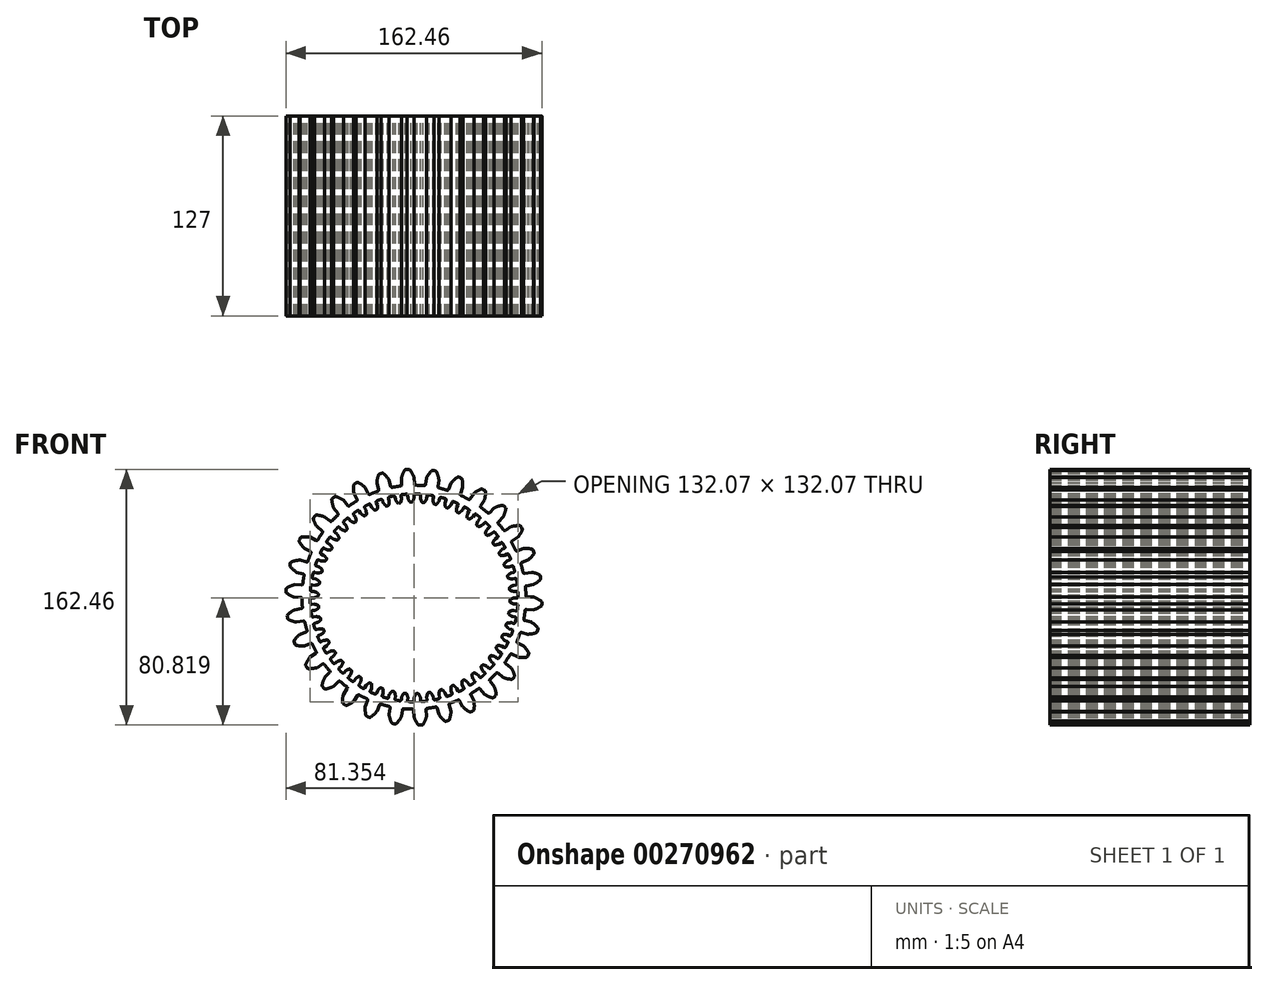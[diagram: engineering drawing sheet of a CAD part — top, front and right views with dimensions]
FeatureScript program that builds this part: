
annotation { "Feature Type Name" : "Feature", "Feature Type Description" : "" }
export const myFeature = defineFeature(function(context is Context, id is Id, definition is map)
    precondition{}
    {
        {
            var Q0;
            Q0=qCreatedBy(makeId("Front.planeOp"),FACE);
            var sketch = newSketch(context, id + "F0", { "sketchPlane" : qUnion([Q0])});
            skArc(sketch, "E0", {"start": v(-8.43, 70.62) * mm, "mid": v(-11.13, 70.24) * mm, "end": v(-13.8, 69.77) * mm});
            skArc(sketch, "E1.trimOffspring", {"start": v(0, 76.2) * mm, "mid": v(-1.15, 78.65) * mm, "end": v(-2.64, 80.92) * mm});
            skLineSegment(sketch, "E2", {"start": v(0, 76.2) * mm, "end": v(0.23, 71.86) * mm});
            skLineSegment(sketch, "E3", {"start": v(-3.26, 81.23) * mm, "end": v(-4.26, 81.23) * mm});
            skLineSegment(sketch, "E4.MirrorCS", {"start": v(-5.25, 81.13) * mm, "end": v(-4.26, 81.23) * mm});
            skArc(sketch, "E5.MirrorCS", {"start": v(-7.97, 75.78) * mm, "mid": v(-7.08, 78.34) * mm, "end": v(-5.84, 80.75) * mm});
            skLineSegment(sketch, "E6.MirrorCS", {"start": v(-7.97, 75.78) * mm, "end": v(-7.74, 71.44) * mm});
            skPoint(sketch, "E7.orphan", {"position": v(-7.45, 65.87) * mm});
            skPoint(sketch, "E8.orphan", {"position": v(0.52, 66.28) * mm});
            skPoint(sketch, "E9.visualSharp", {"position": v(-7.7, 70.7) * mm});
            skArc(sketch, "E9.filletArc", {"start": v(-8.43, 70.62) * mm, "mid": v(-7.92, 70.9) * mm, "end": v(-7.74, 71.44) * mm});
            skPoint(sketch, "E10.visualSharp", {"position": v(0.27, 71.12) * mm});
            skArc(sketch, "E10.filletArc", {"start": v(0.23, 71.86) * mm, "mid": v(0.47, 71.33) * mm, "end": v(1, 71.11) * mm});
            skPoint(sketch, "E11.visualSharp", {"position": v(-2.88, 81.23) * mm});
            skArc(sketch, "E11.filletArc", {"start": v(-2.64, 80.92) * mm, "mid": v(-2.91, 81.15) * mm, "end": v(-3.26, 81.23) * mm});
            skPoint(sketch, "E12.visualSharp", {"position": v(-5.63, 81.08) * mm});
            skArc(sketch, "E12.filletArc", {"start": v(-5.25, 81.13) * mm, "mid": v(-5.58, 81) * mm, "end": v(-5.84, 80.75) * mm});
            skArc(sketch, "E13.1.0", {"start": v(-22.93, 67.32) * mm, "mid": v(-22.49, 67.7) * mm, "end": v(-22.42, 68.27) * mm});
            skLineSegment(sketch, "E13.1.1", {"start": v(-23.55, 72.47) * mm, "end": v(-22.42, 68.27) * mm});
            skArc(sketch, "E13.1.2", {"start": v(-23.55, 72.47) * mm, "mid": v(-23.21, 75.16) * mm, "end": v(-22.5, 77.77) * mm});
            skArc(sketch, "E13.1.3", {"start": v(-22, 78.26) * mm, "mid": v(-22.3, 78.08) * mm, "end": v(-22.5, 77.77) * mm});
            skLineSegment(sketch, "E13.1.4", {"start": v(-22, 78.26) * mm, "end": v(-21.05, 78.57) * mm});
            skLineSegment(sketch, "E13.1.5", {"start": v(-20.08, 78.78) * mm, "end": v(-21.05, 78.57) * mm});
            skArc(sketch, "E13.1.6", {"start": v(-19.4, 78.6) * mm, "mid": v(-19.72, 78.77) * mm, "end": v(-20.08, 78.78) * mm});
            skArc(sketch, "E13.1.7", {"start": v(-15.84, 74.53) * mm, "mid": v(-17.48, 76.7) * mm, "end": v(-19.4, 78.6) * mm});
            skLineSegment(sketch, "E13.1.8", {"start": v(-15.84, 74.53) * mm, "end": v(-14.72, 70.34) * mm});
            skArc(sketch, "E13.1.9", {"start": v(-14.72, 70.34) * mm, "mid": v(-14.37, 69.87) * mm, "end": v(-13.8, 69.77) * mm});
            skArc(sketch, "E13.2.0", {"start": v(-36.42, 61.08) * mm, "mid": v(-36.07, 61.54) * mm, "end": v(-36.13, 62.12) * mm});
            skLineSegment(sketch, "E13.2.1", {"start": v(-38.1, 66) * mm, "end": v(-36.13, 62.12) * mm});
            skArc(sketch, "E13.2.2", {"start": v(-38.1, 66) * mm, "mid": v(-38.33, 68.7) * mm, "end": v(-38.18, 71.4) * mm});
            skArc(sketch, "E13.2.3", {"start": v(-37.79, 71.98) * mm, "mid": v(-38.05, 71.73) * mm, "end": v(-38.18, 71.4) * mm});
            skLineSegment(sketch, "E13.2.4", {"start": v(-37.79, 71.98) * mm, "end": v(-36.93, 72.47) * mm});
            skLineSegment(sketch, "E13.2.5", {"start": v(-36.02, 72.88) * mm, "end": v(-36.93, 72.47) * mm});
            skArc(sketch, "E13.2.6", {"start": v(-35.32, 72.85) * mm, "mid": v(-35.67, 72.95) * mm, "end": v(-36.02, 72.88) * mm});
            skArc(sketch, "E13.2.7", {"start": v(-31, 69.61) * mm, "mid": v(-33.04, 71.39) * mm, "end": v(-35.32, 72.85) * mm});
            skLineSegment(sketch, "E13.2.8", {"start": v(-31, 69.61) * mm, "end": v(-29.02, 65.74) * mm});
            skArc(sketch, "E13.2.9", {"start": v(-29.02, 65.74) * mm, "mid": v(-28.59, 65.36) * mm, "end": v(-28, 65.37) * mm});
            skArc(sketch, "E13.3.0", {"start": v(-48.33, 52.18) * mm, "mid": v(-48.08, 52.7) * mm, "end": v(-48.25, 53.25) * mm});
            skLineSegment(sketch, "E13.3.1", {"start": v(-50.99, 56.63) * mm, "end": v(-48.25, 53.25) * mm});
            skArc(sketch, "E13.3.2", {"start": v(-50.99, 56.63) * mm, "mid": v(-51.77, 59.22) * mm, "end": v(-52.19, 61.9) * mm});
            skArc(sketch, "E13.3.3", {"start": v(-51.93, 62.55) * mm, "mid": v(-52.13, 62.25) * mm, "end": v(-52.19, 61.9) * mm});
            skLineSegment(sketch, "E13.3.4", {"start": v(-51.93, 62.55) * mm, "end": v(-51.19, 63.21) * mm});
            skLineSegment(sketch, "E13.3.5", {"start": v(-50.38, 63.8) * mm, "end": v(-51.19, 63.21) * mm});
            skArc(sketch, "E13.3.6", {"start": v(-49.7, 63.92) * mm, "mid": v(-50.05, 63.94) * mm, "end": v(-50.38, 63.8) * mm});
            skArc(sketch, "E13.3.7", {"start": v(-44.79, 61.65) * mm, "mid": v(-47.16, 62.96) * mm, "end": v(-49.7, 63.92) * mm});
            skLineSegment(sketch, "E13.3.8", {"start": v(-44.79, 61.65) * mm, "end": v(-42.05, 58.27) * mm});
            skArc(sketch, "E13.3.9", {"start": v(-42.05, 58.27) * mm, "mid": v(-41.55, 57.98) * mm, "end": v(-40.99, 58.12) * mm});
            skArc(sketch, "E13.4.0", {"start": v(-58.12, 40.99) * mm, "mid": v(-57.98, 41.55) * mm, "end": v(-58.27, 42.05) * mm});
            skLineSegment(sketch, "E13.4.1", {"start": v(-61.65, 44.79) * mm, "end": v(-58.27, 42.05) * mm});
            skArc(sketch, "E13.4.2", {"start": v(-61.65, 44.79) * mm, "mid": v(-62.96, 47.16) * mm, "end": v(-63.92, 49.7) * mm});
            skArc(sketch, "E13.4.3", {"start": v(-63.8, 50.38) * mm, "mid": v(-63.94, 50.05) * mm, "end": v(-63.92, 49.7) * mm});
            skLineSegment(sketch, "E13.4.4", {"start": v(-63.8, 50.38) * mm, "end": v(-63.21, 51.19) * mm});
            skLineSegment(sketch, "E13.4.5", {"start": v(-62.55, 51.93) * mm, "end": v(-63.21, 51.19) * mm});
            skArc(sketch, "E13.4.6", {"start": v(-61.9, 52.19) * mm, "mid": v(-62.25, 52.13) * mm, "end": v(-62.55, 51.93) * mm});
            skArc(sketch, "E13.4.7", {"start": v(-56.63, 50.99) * mm, "mid": v(-59.22, 51.77) * mm, "end": v(-61.9, 52.19) * mm});
            skLineSegment(sketch, "E13.4.8", {"start": v(-56.63, 50.99) * mm, "end": v(-53.25, 48.25) * mm});
            skArc(sketch, "E13.4.9", {"start": v(-53.25, 48.25) * mm, "mid": v(-52.7, 48.08) * mm, "end": v(-52.18, 48.33) * mm});
            skArc(sketch, "E13.5.0", {"start": v(-65.37, 28) * mm, "mid": v(-65.36, 28.59) * mm, "end": v(-65.74, 29.02) * mm});
            skLineSegment(sketch, "E13.5.1", {"start": v(-69.61, 31) * mm, "end": v(-65.74, 29.02) * mm});
            skArc(sketch, "E13.5.2", {"start": v(-69.61, 31) * mm, "mid": v(-71.39, 33.04) * mm, "end": v(-72.85, 35.32) * mm});
            skArc(sketch, "E13.5.3", {"start": v(-72.88, 36.02) * mm, "mid": v(-72.95, 35.67) * mm, "end": v(-72.85, 35.32) * mm});
            skLineSegment(sketch, "E13.5.4", {"start": v(-72.88, 36.02) * mm, "end": v(-72.47, 36.93) * mm});
            skLineSegment(sketch, "E13.5.5", {"start": v(-71.98, 37.79) * mm, "end": v(-72.47, 36.93) * mm});
            skArc(sketch, "E13.5.6", {"start": v(-71.4, 38.18) * mm, "mid": v(-71.73, 38.05) * mm, "end": v(-71.98, 37.79) * mm});
            skArc(sketch, "E13.5.7", {"start": v(-66, 38.1) * mm, "mid": v(-68.7, 38.33) * mm, "end": v(-71.4, 38.18) * mm});
            skLineSegment(sketch, "E13.5.8", {"start": v(-66, 38.1) * mm, "end": v(-62.12, 36.13) * mm});
            skArc(sketch, "E13.5.9", {"start": v(-62.12, 36.13) * mm, "mid": v(-61.54, 36.07) * mm, "end": v(-61.08, 36.42) * mm});
            skArc(sketch, "E13.6.0", {"start": v(-69.77, 13.8) * mm, "mid": v(-69.87, 14.37) * mm, "end": v(-70.34, 14.72) * mm});
            skLineSegment(sketch, "E13.6.1", {"start": v(-74.53, 15.84) * mm, "end": v(-70.34, 14.72) * mm});
            skArc(sketch, "E13.6.2", {"start": v(-74.53, 15.84) * mm, "mid": v(-76.7, 17.48) * mm, "end": v(-78.6, 19.4) * mm});
            skArc(sketch, "E13.6.3", {"start": v(-78.78, 20.08) * mm, "mid": v(-78.77, 19.72) * mm, "end": v(-78.6, 19.4) * mm});
            skLineSegment(sketch, "E13.6.4", {"start": v(-78.78, 20.08) * mm, "end": v(-78.57, 21.05) * mm});
            skLineSegment(sketch, "E13.6.5", {"start": v(-78.26, 22) * mm, "end": v(-78.57, 21.05) * mm});
            skArc(sketch, "E13.6.6", {"start": v(-77.77, 22.5) * mm, "mid": v(-78.08, 22.3) * mm, "end": v(-78.26, 22) * mm});
            skArc(sketch, "E13.6.7", {"start": v(-72.47, 23.55) * mm, "mid": v(-75.16, 23.21) * mm, "end": v(-77.77, 22.5) * mm});
            skLineSegment(sketch, "E13.6.8", {"start": v(-72.47, 23.55) * mm, "end": v(-68.27, 22.42) * mm});
            skArc(sketch, "E13.6.9", {"start": v(-68.27, 22.42) * mm, "mid": v(-67.7, 22.49) * mm, "end": v(-67.32, 22.93) * mm});
            skArc(sketch, "E13.7.0", {"start": v(-71.11, -1) * mm, "mid": v(-71.33, -0.47) * mm, "end": v(-71.86, -0.23) * mm});
            skLineSegment(sketch, "E13.7.1", {"start": v(-76.2, 0) * mm, "end": v(-71.86, -0.23) * mm});
            skArc(sketch, "E13.7.2", {"start": v(-76.2, 0) * mm, "mid": v(-78.65, 1.15) * mm, "end": v(-80.92, 2.64) * mm});
            skArc(sketch, "E13.7.3", {"start": v(-81.23, 3.26) * mm, "mid": v(-81.15, 2.91) * mm, "end": v(-80.92, 2.64) * mm});
            skLineSegment(sketch, "E13.7.4", {"start": v(-81.23, 3.26) * mm, "end": v(-81.23, 4.26) * mm});
            skLineSegment(sketch, "E13.7.5", {"start": v(-81.13, 5.25) * mm, "end": v(-81.23, 4.26) * mm});
            skArc(sketch, "E13.7.6", {"start": v(-80.75, 5.84) * mm, "mid": v(-81, 5.58) * mm, "end": v(-81.13, 5.25) * mm});
            skArc(sketch, "E13.7.7", {"start": v(-75.78, 7.97) * mm, "mid": v(-78.34, 7.08) * mm, "end": v(-80.75, 5.84) * mm});
            skLineSegment(sketch, "E13.7.8", {"start": v(-75.78, 7.97) * mm, "end": v(-71.44, 7.74) * mm});
            skArc(sketch, "E13.7.9", {"start": v(-71.44, 7.74) * mm, "mid": v(-70.9, 7.92) * mm, "end": v(-70.62, 8.43) * mm});
            skArc(sketch, "E13.8.0", {"start": v(-69.35, -15.77) * mm, "mid": v(-69.68, -15.29) * mm, "end": v(-70.24, -15.16) * mm});
            skLineSegment(sketch, "E13.8.1", {"start": v(-74.53, -15.84) * mm, "end": v(-70.24, -15.16) * mm});
            skArc(sketch, "E13.8.2", {"start": v(-74.53, -15.84) * mm, "mid": v(-77.17, -15.23) * mm, "end": v(-79.7, -14.24) * mm});
            skArc(sketch, "E13.8.3", {"start": v(-80.13, -13.7) * mm, "mid": v(-79.98, -14.02) * mm, "end": v(-79.7, -14.24) * mm});
            skLineSegment(sketch, "E13.8.4", {"start": v(-80.13, -13.7) * mm, "end": v(-80.34, -12.72) * mm});
            skLineSegment(sketch, "E13.8.5", {"start": v(-80.44, -11.74) * mm, "end": v(-80.34, -12.72) * mm});
            skArc(sketch, "E13.8.6", {"start": v(-80.2, -11.08) * mm, "mid": v(-80.4, -11.38) * mm, "end": v(-80.44, -11.74) * mm});
            skArc(sketch, "E13.8.7", {"start": v(-75.78, -7.97) * mm, "mid": v(-78.1, -9.37) * mm, "end": v(-80.2, -11.08) * mm});
            skLineSegment(sketch, "E13.8.8", {"start": v(-75.78, -7.97) * mm, "end": v(-71.49, -7.29) * mm});
            skArc(sketch, "E13.8.9", {"start": v(-71.49, -7.29) * mm, "mid": v(-71, -7) * mm, "end": v(-70.83, -6.44) * mm});
            skArc(sketch, "E13.9.0", {"start": v(-64.56, -29.84) * mm, "mid": v(-64.98, -29.44) * mm, "end": v(-65.55, -29.44) * mm});
            skLineSegment(sketch, "E13.9.1", {"start": v(-69.61, -31) * mm, "end": v(-65.55, -29.44) * mm});
            skArc(sketch, "E13.9.2", {"start": v(-69.61, -31) * mm, "mid": v(-72.32, -30.94) * mm, "end": v(-75, -30.5) * mm});
            skArc(sketch, "E13.9.3", {"start": v(-75.53, -30.06) * mm, "mid": v(-75.32, -30.34) * mm, "end": v(-75, -30.5) * mm});
            skLineSegment(sketch, "E13.9.4", {"start": v(-75.53, -30.06) * mm, "end": v(-75.94, -29.15) * mm});
            skLineSegment(sketch, "E13.9.5", {"start": v(-76.25, -28.2) * mm, "end": v(-75.94, -29.15) * mm});
            skArc(sketch, "E13.9.6", {"start": v(-76.14, -27.51) * mm, "mid": v(-76.28, -27.85) * mm, "end": v(-76.25, -28.2) * mm});
            skArc(sketch, "E13.9.7", {"start": v(-72.47, -23.55) * mm, "mid": v(-74.45, -25.4) * mm, "end": v(-76.14, -27.51) * mm});
            skLineSegment(sketch, "E13.9.8", {"start": v(-72.47, -23.55) * mm, "end": v(-68.41, -21.99) * mm});
            skArc(sketch, "E13.9.9", {"start": v(-68.41, -21.99) * mm, "mid": v(-67.99, -21.6) * mm, "end": v(-67.94, -21.02) * mm});
            skArc(sketch, "E13.10.0", {"start": v(-56.94, -42.61) * mm, "mid": v(-57.43, -42.3) * mm, "end": v(-58, -42.42) * mm});
            skLineSegment(sketch, "E13.10.1", {"start": v(-61.65, -44.79) * mm, "end": v(-58, -42.42) * mm});
            skArc(sketch, "E13.10.2", {"start": v(-61.65, -44.79) * mm, "mid": v(-64.3, -45.3) * mm, "end": v(-67.01, -45.43) * mm});
            skArc(sketch, "E13.10.3", {"start": v(-67.63, -45.1) * mm, "mid": v(-67.36, -45.34) * mm, "end": v(-67.01, -45.43) * mm});
            skLineSegment(sketch, "E13.10.4", {"start": v(-67.63, -45.1) * mm, "end": v(-68.22, -44.3) * mm});
            skLineSegment(sketch, "E13.10.5", {"start": v(-68.72, -43.44) * mm, "end": v(-68.22, -44.3) * mm});
            skArc(sketch, "E13.10.6", {"start": v(-68.76, -42.74) * mm, "mid": v(-68.82, -43.1) * mm, "end": v(-68.72, -43.44) * mm});
            skArc(sketch, "E13.10.7", {"start": v(-66, -38.1) * mm, "mid": v(-67.54, -40.32) * mm, "end": v(-68.76, -42.74) * mm});
            skLineSegment(sketch, "E13.10.8", {"start": v(-66, -38.1) * mm, "end": v(-62.35, -35.73) * mm});
            skArc(sketch, "E13.10.9", {"start": v(-62.35, -35.73) * mm, "mid": v(-62.01, -35.26) * mm, "end": v(-62.09, -34.69) * mm});
            skArc(sketch, "E13.11.0", {"start": v(-46.84, -53.52) * mm, "mid": v(-47.38, -53.32) * mm, "end": v(-47.91, -53.55) * mm});
            skLineSegment(sketch, "E13.11.1", {"start": v(-50.99, -56.63) * mm, "end": v(-47.91, -53.55) * mm});
            skArc(sketch, "E13.11.2", {"start": v(-50.99, -56.63) * mm, "mid": v(-53.48, -57.68) * mm, "end": v(-56.1, -58.37) * mm});
            skArc(sketch, "E13.11.3", {"start": v(-56.78, -58.18) * mm, "mid": v(-56.46, -58.35) * mm, "end": v(-56.1, -58.37) * mm});
            skLineSegment(sketch, "E13.11.4", {"start": v(-56.78, -58.18) * mm, "end": v(-57.52, -57.52) * mm});
            skLineSegment(sketch, "E13.11.5", {"start": v(-58.18, -56.78) * mm, "end": v(-57.52, -57.52) * mm});
            skArc(sketch, "E13.11.6", {"start": v(-58.37, -56.1) * mm, "mid": v(-58.35, -56.46) * mm, "end": v(-58.18, -56.78) * mm});
            skArc(sketch, "E13.11.7", {"start": v(-56.63, -50.99) * mm, "mid": v(-57.68, -53.48) * mm, "end": v(-58.37, -56.1) * mm});
            skLineSegment(sketch, "E13.11.8", {"start": v(-56.63, -50.99) * mm, "end": v(-53.55, -47.91) * mm});
            skArc(sketch, "E13.11.9", {"start": v(-53.55, -47.91) * mm, "mid": v(-53.32, -47.38) * mm, "end": v(-53.52, -46.84) * mm});
            skArc(sketch, "E13.12.0", {"start": v(-34.69, -62.09) * mm, "mid": v(-35.26, -62.01) * mm, "end": v(-35.73, -62.35) * mm});
            skLineSegment(sketch, "E13.12.1", {"start": v(-38.1, -66) * mm, "end": v(-35.73, -62.35) * mm});
            skArc(sketch, "E13.12.2", {"start": v(-38.1, -66) * mm, "mid": v(-40.32, -67.54) * mm, "end": v(-42.74, -68.76) * mm});
            skArc(sketch, "E13.12.3", {"start": v(-43.44, -68.72) * mm, "mid": v(-43.1, -68.82) * mm, "end": v(-42.74, -68.76) * mm});
            skLineSegment(sketch, "E13.12.4", {"start": v(-43.44, -68.72) * mm, "end": v(-44.3, -68.22) * mm});
            skLineSegment(sketch, "E13.12.5", {"start": v(-45.1, -67.63) * mm, "end": v(-44.3, -68.22) * mm});
            skArc(sketch, "E13.12.6", {"start": v(-45.43, -67.01) * mm, "mid": v(-45.34, -67.36) * mm, "end": v(-45.1, -67.63) * mm});
            skArc(sketch, "E13.12.7", {"start": v(-44.79, -61.65) * mm, "mid": v(-45.3, -64.3) * mm, "end": v(-45.43, -67.01) * mm});
            skLineSegment(sketch, "E13.12.8", {"start": v(-44.79, -61.65) * mm, "end": v(-42.42, -58) * mm});
            skArc(sketch, "E13.12.9", {"start": v(-42.42, -58) * mm, "mid": v(-42.3, -57.43) * mm, "end": v(-42.61, -56.94) * mm});
            skArc(sketch, "E13.13.0", {"start": v(-21.02, -67.94) * mm, "mid": v(-21.6, -67.99) * mm, "end": v(-21.99, -68.41) * mm});
            skLineSegment(sketch, "E13.13.1", {"start": v(-23.55, -72.47) * mm, "end": v(-21.99, -68.41) * mm});
            skArc(sketch, "E13.13.2", {"start": v(-23.55, -72.47) * mm, "mid": v(-25.4, -74.45) * mm, "end": v(-27.51, -76.14) * mm});
            skArc(sketch, "E13.13.3", {"start": v(-28.2, -76.25) * mm, "mid": v(-27.85, -76.28) * mm, "end": v(-27.51, -76.14) * mm});
            skLineSegment(sketch, "E13.13.4", {"start": v(-28.2, -76.25) * mm, "end": v(-29.15, -75.94) * mm});
            skLineSegment(sketch, "E13.13.5", {"start": v(-30.06, -75.53) * mm, "end": v(-29.15, -75.94) * mm});
            skArc(sketch, "E13.13.6", {"start": v(-30.5, -75) * mm, "mid": v(-30.34, -75.32) * mm, "end": v(-30.06, -75.53) * mm});
            skArc(sketch, "E13.13.7", {"start": v(-31, -69.61) * mm, "mid": v(-30.94, -72.32) * mm, "end": v(-30.5, -75) * mm});
            skLineSegment(sketch, "E13.13.8", {"start": v(-31, -69.61) * mm, "end": v(-29.44, -65.55) * mm});
            skArc(sketch, "E13.13.9", {"start": v(-29.44, -65.55) * mm, "mid": v(-29.44, -64.98) * mm, "end": v(-29.84, -64.56) * mm});
            skArc(sketch, "E13.14.0", {"start": v(-6.44, -70.83) * mm, "mid": v(-7, -71) * mm, "end": v(-7.29, -71.49) * mm});
            skLineSegment(sketch, "E13.14.1", {"start": v(-7.97, -75.78) * mm, "end": v(-7.29, -71.49) * mm});
            skArc(sketch, "E13.14.2", {"start": v(-7.97, -75.78) * mm, "mid": v(-9.37, -78.1) * mm, "end": v(-11.08, -80.2) * mm});
            skArc(sketch, "E13.14.3", {"start": v(-11.74, -80.44) * mm, "mid": v(-11.38, -80.4) * mm, "end": v(-11.08, -80.2) * mm});
            skLineSegment(sketch, "E13.14.4", {"start": v(-11.74, -80.44) * mm, "end": v(-12.72, -80.34) * mm});
            skLineSegment(sketch, "E13.14.5", {"start": v(-13.7, -80.13) * mm, "end": v(-12.72, -80.34) * mm});
            skArc(sketch, "E13.14.6", {"start": v(-14.24, -79.7) * mm, "mid": v(-14.02, -79.98) * mm, "end": v(-13.7, -80.13) * mm});
            skArc(sketch, "E13.14.7", {"start": v(-15.84, -74.53) * mm, "mid": v(-15.23, -77.17) * mm, "end": v(-14.24, -79.7) * mm});
            skLineSegment(sketch, "E13.14.8", {"start": v(-15.84, -74.53) * mm, "end": v(-15.16, -70.24) * mm});
            skArc(sketch, "E13.14.9", {"start": v(-15.16, -70.24) * mm, "mid": v(-15.29, -69.68) * mm, "end": v(-15.77, -69.35) * mm});
            skArc(sketch, "E13.15.0", {"start": v(8.43, -70.62) * mm, "mid": v(7.92, -70.9) * mm, "end": v(7.74, -71.44) * mm});
            skLineSegment(sketch, "E13.15.1", {"start": v(7.97, -75.78) * mm, "end": v(7.74, -71.44) * mm});
            skArc(sketch, "E13.15.2", {"start": v(7.97, -75.78) * mm, "mid": v(7.08, -78.34) * mm, "end": v(5.84, -80.75) * mm});
            skArc(sketch, "E13.15.3", {"start": v(5.25, -81.13) * mm, "mid": v(5.58, -81) * mm, "end": v(5.84, -80.75) * mm});
            skLineSegment(sketch, "E13.15.4", {"start": v(5.25, -81.13) * mm, "end": v(4.26, -81.23) * mm});
            skLineSegment(sketch, "E13.15.5", {"start": v(3.26, -81.23) * mm, "end": v(4.26, -81.23) * mm});
            skArc(sketch, "E13.15.6", {"start": v(2.64, -80.92) * mm, "mid": v(2.91, -81.15) * mm, "end": v(3.26, -81.23) * mm});
            skArc(sketch, "E13.15.7", {"start": v(0, -76.2) * mm, "mid": v(1.15, -78.65) * mm, "end": v(2.64, -80.92) * mm});
            skLineSegment(sketch, "E13.15.8", {"start": v(0, -76.2) * mm, "end": v(-0.23, -71.86) * mm});
            skArc(sketch, "E13.15.9", {"start": v(-0.23, -71.86) * mm, "mid": v(-0.47, -71.33) * mm, "end": v(-1, -71.11) * mm});
            skArc(sketch, "E13.16.0", {"start": v(22.93, -67.32) * mm, "mid": v(22.49, -67.7) * mm, "end": v(22.42, -68.27) * mm});
            skLineSegment(sketch, "E13.16.1", {"start": v(23.55, -72.47) * mm, "end": v(22.42, -68.27) * mm});
            skArc(sketch, "E13.16.2", {"start": v(23.55, -72.47) * mm, "mid": v(23.21, -75.16) * mm, "end": v(22.5, -77.77) * mm});
            skArc(sketch, "E13.16.3", {"start": v(22, -78.26) * mm, "mid": v(22.3, -78.08) * mm, "end": v(22.5, -77.77) * mm});
            skLineSegment(sketch, "E13.16.4", {"start": v(22, -78.26) * mm, "end": v(21.05, -78.57) * mm});
            skLineSegment(sketch, "E13.16.5", {"start": v(20.08, -78.78) * mm, "end": v(21.05, -78.57) * mm});
            skArc(sketch, "E13.16.6", {"start": v(19.4, -78.6) * mm, "mid": v(19.72, -78.77) * mm, "end": v(20.08, -78.78) * mm});
            skArc(sketch, "E13.16.7", {"start": v(15.84, -74.53) * mm, "mid": v(17.48, -76.7) * mm, "end": v(19.4, -78.6) * mm});
            skLineSegment(sketch, "E13.16.8", {"start": v(15.84, -74.53) * mm, "end": v(14.72, -70.34) * mm});
            skArc(sketch, "E13.16.9", {"start": v(14.72, -70.34) * mm, "mid": v(14.37, -69.87) * mm, "end": v(13.8, -69.77) * mm});
            skArc(sketch, "E13.17.0", {"start": v(36.42, -61.08) * mm, "mid": v(36.07, -61.54) * mm, "end": v(36.13, -62.12) * mm});
            skLineSegment(sketch, "E13.17.1", {"start": v(38.1, -66) * mm, "end": v(36.13, -62.12) * mm});
            skArc(sketch, "E13.17.2", {"start": v(38.1, -66) * mm, "mid": v(38.33, -68.7) * mm, "end": v(38.18, -71.4) * mm});
            skArc(sketch, "E13.17.3", {"start": v(37.79, -71.98) * mm, "mid": v(38.05, -71.73) * mm, "end": v(38.18, -71.4) * mm});
            skLineSegment(sketch, "E13.17.4", {"start": v(37.79, -71.98) * mm, "end": v(36.93, -72.47) * mm});
            skLineSegment(sketch, "E13.17.5", {"start": v(36.02, -72.88) * mm, "end": v(36.93, -72.47) * mm});
            skArc(sketch, "E13.17.6", {"start": v(35.32, -72.85) * mm, "mid": v(35.67, -72.95) * mm, "end": v(36.02, -72.88) * mm});
            skArc(sketch, "E13.17.7", {"start": v(31, -69.61) * mm, "mid": v(33.04, -71.39) * mm, "end": v(35.32, -72.85) * mm});
            skLineSegment(sketch, "E13.17.8", {"start": v(31, -69.61) * mm, "end": v(29.02, -65.74) * mm});
            skArc(sketch, "E13.17.9", {"start": v(29.02, -65.74) * mm, "mid": v(28.59, -65.36) * mm, "end": v(28, -65.37) * mm});
            skArc(sketch, "E13.18.0", {"start": v(48.33, -52.18) * mm, "mid": v(48.08, -52.7) * mm, "end": v(48.25, -53.25) * mm});
            skLineSegment(sketch, "E13.18.1", {"start": v(50.99, -56.63) * mm, "end": v(48.25, -53.25) * mm});
            skArc(sketch, "E13.18.2", {"start": v(50.99, -56.63) * mm, "mid": v(51.77, -59.22) * mm, "end": v(52.19, -61.9) * mm});
            skArc(sketch, "E13.18.3", {"start": v(51.93, -62.55) * mm, "mid": v(52.13, -62.25) * mm, "end": v(52.19, -61.9) * mm});
            skLineSegment(sketch, "E13.18.4", {"start": v(51.93, -62.55) * mm, "end": v(51.19, -63.21) * mm});
            skLineSegment(sketch, "E13.18.5", {"start": v(50.38, -63.8) * mm, "end": v(51.19, -63.21) * mm});
            skArc(sketch, "E13.18.6", {"start": v(49.7, -63.92) * mm, "mid": v(50.05, -63.94) * mm, "end": v(50.38, -63.8) * mm});
            skArc(sketch, "E13.18.7", {"start": v(44.79, -61.65) * mm, "mid": v(47.16, -62.96) * mm, "end": v(49.7, -63.92) * mm});
            skLineSegment(sketch, "E13.18.8", {"start": v(44.79, -61.65) * mm, "end": v(42.05, -58.27) * mm});
            skArc(sketch, "E13.18.9", {"start": v(42.05, -58.27) * mm, "mid": v(41.55, -57.98) * mm, "end": v(40.99, -58.12) * mm});
            skArc(sketch, "E13.19.0", {"start": v(58.12, -40.99) * mm, "mid": v(57.98, -41.55) * mm, "end": v(58.27, -42.05) * mm});
            skLineSegment(sketch, "E13.19.1", {"start": v(61.65, -44.79) * mm, "end": v(58.27, -42.05) * mm});
            skArc(sketch, "E13.19.2", {"start": v(61.65, -44.79) * mm, "mid": v(62.96, -47.16) * mm, "end": v(63.92, -49.7) * mm});
            skArc(sketch, "E13.19.3", {"start": v(63.8, -50.38) * mm, "mid": v(63.94, -50.05) * mm, "end": v(63.92, -49.7) * mm});
            skLineSegment(sketch, "E13.19.4", {"start": v(63.8, -50.38) * mm, "end": v(63.21, -51.19) * mm});
            skLineSegment(sketch, "E13.19.5", {"start": v(62.55, -51.93) * mm, "end": v(63.21, -51.19) * mm});
            skArc(sketch, "E13.19.6", {"start": v(61.9, -52.19) * mm, "mid": v(62.25, -52.13) * mm, "end": v(62.55, -51.93) * mm});
            skArc(sketch, "E13.19.7", {"start": v(56.63, -50.99) * mm, "mid": v(59.22, -51.77) * mm, "end": v(61.9, -52.19) * mm});
            skLineSegment(sketch, "E13.19.8", {"start": v(56.63, -50.99) * mm, "end": v(53.25, -48.25) * mm});
            skArc(sketch, "E13.19.9", {"start": v(53.25, -48.25) * mm, "mid": v(52.7, -48.08) * mm, "end": v(52.18, -48.33) * mm});
            skArc(sketch, "E13.20.0", {"start": v(65.37, -28) * mm, "mid": v(65.36, -28.59) * mm, "end": v(65.74, -29.02) * mm});
            skLineSegment(sketch, "E13.20.1", {"start": v(69.61, -31) * mm, "end": v(65.74, -29.02) * mm});
            skArc(sketch, "E13.20.2", {"start": v(69.61, -31) * mm, "mid": v(71.39, -33.04) * mm, "end": v(72.85, -35.32) * mm});
            skArc(sketch, "E13.20.3", {"start": v(72.88, -36.02) * mm, "mid": v(72.95, -35.67) * mm, "end": v(72.85, -35.32) * mm});
            skLineSegment(sketch, "E13.20.4", {"start": v(72.88, -36.02) * mm, "end": v(72.47, -36.93) * mm});
            skLineSegment(sketch, "E13.20.5", {"start": v(71.98, -37.79) * mm, "end": v(72.47, -36.93) * mm});
            skArc(sketch, "E13.20.6", {"start": v(71.4, -38.18) * mm, "mid": v(71.73, -38.05) * mm, "end": v(71.98, -37.79) * mm});
            skArc(sketch, "E13.20.7", {"start": v(66, -38.1) * mm, "mid": v(68.7, -38.33) * mm, "end": v(71.4, -38.18) * mm});
            skLineSegment(sketch, "E13.20.8", {"start": v(66, -38.1) * mm, "end": v(62.12, -36.13) * mm});
            skArc(sketch, "E13.20.9", {"start": v(62.12, -36.13) * mm, "mid": v(61.54, -36.07) * mm, "end": v(61.08, -36.42) * mm});
            skArc(sketch, "E13.21.0", {"start": v(69.77, -13.8) * mm, "mid": v(69.87, -14.37) * mm, "end": v(70.34, -14.72) * mm});
            skLineSegment(sketch, "E13.21.1", {"start": v(74.53, -15.84) * mm, "end": v(70.34, -14.72) * mm});
            skArc(sketch, "E13.21.2", {"start": v(74.53, -15.84) * mm, "mid": v(76.7, -17.48) * mm, "end": v(78.6, -19.4) * mm});
            skArc(sketch, "E13.21.3", {"start": v(78.78, -20.08) * mm, "mid": v(78.77, -19.72) * mm, "end": v(78.6, -19.4) * mm});
            skLineSegment(sketch, "E13.21.4", {"start": v(78.78, -20.08) * mm, "end": v(78.57, -21.05) * mm});
            skLineSegment(sketch, "E13.21.5", {"start": v(78.26, -22) * mm, "end": v(78.57, -21.05) * mm});
            skArc(sketch, "E13.21.6", {"start": v(77.77, -22.5) * mm, "mid": v(78.08, -22.3) * mm, "end": v(78.26, -22) * mm});
            skArc(sketch, "E13.21.7", {"start": v(72.47, -23.55) * mm, "mid": v(75.16, -23.21) * mm, "end": v(77.77, -22.5) * mm});
            skLineSegment(sketch, "E13.21.8", {"start": v(72.47, -23.55) * mm, "end": v(68.27, -22.42) * mm});
            skArc(sketch, "E13.21.9", {"start": v(68.27, -22.42) * mm, "mid": v(67.7, -22.49) * mm, "end": v(67.32, -22.93) * mm});
            skArc(sketch, "E13.22.0", {"start": v(71.11, 1) * mm, "mid": v(71.33, 0.47) * mm, "end": v(71.86, 0.23) * mm});
            skLineSegment(sketch, "E13.22.1", {"start": v(76.2, 0) * mm, "end": v(71.86, 0.23) * mm});
            skArc(sketch, "E13.22.2", {"start": v(76.2, 0) * mm, "mid": v(78.65, -1.15) * mm, "end": v(80.92, -2.64) * mm});
            skArc(sketch, "E13.22.3", {"start": v(81.23, -3.26) * mm, "mid": v(81.15, -2.91) * mm, "end": v(80.92, -2.64) * mm});
            skLineSegment(sketch, "E13.22.4", {"start": v(81.23, -3.26) * mm, "end": v(81.23, -4.26) * mm});
            skLineSegment(sketch, "E13.22.5", {"start": v(81.13, -5.25) * mm, "end": v(81.23, -4.26) * mm});
            skArc(sketch, "E13.22.6", {"start": v(80.75, -5.84) * mm, "mid": v(81, -5.58) * mm, "end": v(81.13, -5.25) * mm});
            skArc(sketch, "E13.22.7", {"start": v(75.78, -7.97) * mm, "mid": v(78.34, -7.08) * mm, "end": v(80.75, -5.84) * mm});
            skLineSegment(sketch, "E13.22.8", {"start": v(75.78, -7.97) * mm, "end": v(71.44, -7.74) * mm});
            skArc(sketch, "E13.22.9", {"start": v(71.44, -7.74) * mm, "mid": v(70.9, -7.92) * mm, "end": v(70.62, -8.43) * mm});
            skArc(sketch, "E13.23.0", {"start": v(69.35, 15.77) * mm, "mid": v(69.68, 15.29) * mm, "end": v(70.24, 15.16) * mm});
            skLineSegment(sketch, "E13.23.1", {"start": v(74.53, 15.84) * mm, "end": v(70.24, 15.16) * mm});
            skArc(sketch, "E13.23.2", {"start": v(74.53, 15.84) * mm, "mid": v(77.17, 15.23) * mm, "end": v(79.7, 14.24) * mm});
            skArc(sketch, "E13.23.3", {"start": v(80.13, 13.7) * mm, "mid": v(79.98, 14.02) * mm, "end": v(79.7, 14.24) * mm});
            skLineSegment(sketch, "E13.23.4", {"start": v(80.13, 13.7) * mm, "end": v(80.34, 12.72) * mm});
            skLineSegment(sketch, "E13.23.5", {"start": v(80.44, 11.74) * mm, "end": v(80.34, 12.72) * mm});
            skArc(sketch, "E13.23.6", {"start": v(80.2, 11.08) * mm, "mid": v(80.4, 11.38) * mm, "end": v(80.44, 11.74) * mm});
            skArc(sketch, "E13.23.7", {"start": v(75.78, 7.97) * mm, "mid": v(78.1, 9.37) * mm, "end": v(80.2, 11.08) * mm});
            skLineSegment(sketch, "E13.23.8", {"start": v(75.78, 7.97) * mm, "end": v(71.49, 7.29) * mm});
            skArc(sketch, "E13.23.9", {"start": v(71.49, 7.29) * mm, "mid": v(71, 7) * mm, "end": v(70.83, 6.44) * mm});
            skArc(sketch, "E13.24.0", {"start": v(64.56, 29.84) * mm, "mid": v(64.98, 29.44) * mm, "end": v(65.55, 29.44) * mm});
            skLineSegment(sketch, "E13.24.1", {"start": v(69.61, 31) * mm, "end": v(65.55, 29.44) * mm});
            skArc(sketch, "E13.24.2", {"start": v(69.61, 31) * mm, "mid": v(72.32, 30.94) * mm, "end": v(75, 30.5) * mm});
            skArc(sketch, "E13.24.3", {"start": v(75.53, 30.06) * mm, "mid": v(75.32, 30.34) * mm, "end": v(75, 30.5) * mm});
            skLineSegment(sketch, "E13.24.4", {"start": v(75.53, 30.06) * mm, "end": v(75.94, 29.15) * mm});
            skLineSegment(sketch, "E13.24.5", {"start": v(76.25, 28.2) * mm, "end": v(75.94, 29.15) * mm});
            skArc(sketch, "E13.24.6", {"start": v(76.14, 27.51) * mm, "mid": v(76.28, 27.85) * mm, "end": v(76.25, 28.2) * mm});
            skArc(sketch, "E13.24.7", {"start": v(72.47, 23.55) * mm, "mid": v(74.45, 25.4) * mm, "end": v(76.14, 27.51) * mm});
            skLineSegment(sketch, "E13.24.8", {"start": v(72.47, 23.55) * mm, "end": v(68.41, 21.99) * mm});
            skArc(sketch, "E13.24.9", {"start": v(68.41, 21.99) * mm, "mid": v(67.99, 21.6) * mm, "end": v(67.94, 21.02) * mm});
            skArc(sketch, "E13.25.0", {"start": v(56.94, 42.61) * mm, "mid": v(57.43, 42.3) * mm, "end": v(58, 42.42) * mm});
            skLineSegment(sketch, "E13.25.1", {"start": v(61.65, 44.79) * mm, "end": v(58, 42.42) * mm});
            skArc(sketch, "E13.25.2", {"start": v(61.65, 44.79) * mm, "mid": v(64.3, 45.3) * mm, "end": v(67.01, 45.43) * mm});
            skArc(sketch, "E13.25.3", {"start": v(67.63, 45.1) * mm, "mid": v(67.36, 45.34) * mm, "end": v(67.01, 45.43) * mm});
            skLineSegment(sketch, "E13.25.4", {"start": v(67.63, 45.1) * mm, "end": v(68.22, 44.3) * mm});
            skLineSegment(sketch, "E13.25.5", {"start": v(68.72, 43.44) * mm, "end": v(68.22, 44.3) * mm});
            skArc(sketch, "E13.25.6", {"start": v(68.76, 42.74) * mm, "mid": v(68.82, 43.1) * mm, "end": v(68.72, 43.44) * mm});
            skArc(sketch, "E13.25.7", {"start": v(66, 38.1) * mm, "mid": v(67.54, 40.32) * mm, "end": v(68.76, 42.74) * mm});
            skLineSegment(sketch, "E13.25.8", {"start": v(66, 38.1) * mm, "end": v(62.35, 35.73) * mm});
            skArc(sketch, "E13.25.9", {"start": v(62.35, 35.73) * mm, "mid": v(62.01, 35.26) * mm, "end": v(62.09, 34.69) * mm});
            skArc(sketch, "E13.26.0", {"start": v(46.84, 53.52) * mm, "mid": v(47.38, 53.32) * mm, "end": v(47.91, 53.55) * mm});
            skLineSegment(sketch, "E13.26.1", {"start": v(50.99, 56.63) * mm, "end": v(47.91, 53.55) * mm});
            skArc(sketch, "E13.26.2", {"start": v(50.99, 56.63) * mm, "mid": v(53.48, 57.68) * mm, "end": v(56.1, 58.37) * mm});
            skArc(sketch, "E13.26.3", {"start": v(56.78, 58.18) * mm, "mid": v(56.46, 58.35) * mm, "end": v(56.1, 58.37) * mm});
            skLineSegment(sketch, "E13.26.4", {"start": v(56.78, 58.18) * mm, "end": v(57.52, 57.52) * mm});
            skLineSegment(sketch, "E13.26.5", {"start": v(58.18, 56.78) * mm, "end": v(57.52, 57.52) * mm});
            skArc(sketch, "E13.26.6", {"start": v(58.37, 56.1) * mm, "mid": v(58.35, 56.46) * mm, "end": v(58.18, 56.78) * mm});
            skArc(sketch, "E13.26.7", {"start": v(56.63, 50.99) * mm, "mid": v(57.68, 53.48) * mm, "end": v(58.37, 56.1) * mm});
            skLineSegment(sketch, "E13.26.8", {"start": v(56.63, 50.99) * mm, "end": v(53.55, 47.91) * mm});
            skArc(sketch, "E13.26.9", {"start": v(53.55, 47.91) * mm, "mid": v(53.32, 47.38) * mm, "end": v(53.52, 46.84) * mm});
            skArc(sketch, "E13.27.0", {"start": v(34.69, 62.09) * mm, "mid": v(35.26, 62.01) * mm, "end": v(35.73, 62.35) * mm});
            skLineSegment(sketch, "E13.27.1", {"start": v(38.1, 66) * mm, "end": v(35.73, 62.35) * mm});
            skArc(sketch, "E13.27.2", {"start": v(38.1, 66) * mm, "mid": v(40.32, 67.54) * mm, "end": v(42.74, 68.76) * mm});
            skArc(sketch, "E13.27.3", {"start": v(43.44, 68.72) * mm, "mid": v(43.1, 68.82) * mm, "end": v(42.74, 68.76) * mm});
            skLineSegment(sketch, "E13.27.4", {"start": v(43.44, 68.72) * mm, "end": v(44.3, 68.22) * mm});
            skLineSegment(sketch, "E13.27.5", {"start": v(45.1, 67.63) * mm, "end": v(44.3, 68.22) * mm});
            skArc(sketch, "E13.27.6", {"start": v(45.43, 67.01) * mm, "mid": v(45.34, 67.36) * mm, "end": v(45.1, 67.63) * mm});
            skArc(sketch, "E13.27.7", {"start": v(44.79, 61.65) * mm, "mid": v(45.3, 64.3) * mm, "end": v(45.43, 67.01) * mm});
            skLineSegment(sketch, "E13.27.8", {"start": v(44.79, 61.65) * mm, "end": v(42.42, 58) * mm});
            skArc(sketch, "E13.27.9", {"start": v(42.42, 58) * mm, "mid": v(42.3, 57.43) * mm, "end": v(42.61, 56.94) * mm});
            skArc(sketch, "E13.28.0", {"start": v(21.02, 67.94) * mm, "mid": v(21.6, 67.99) * mm, "end": v(21.99, 68.41) * mm});
            skLineSegment(sketch, "E13.28.1", {"start": v(23.55, 72.47) * mm, "end": v(21.99, 68.41) * mm});
            skArc(sketch, "E13.28.2", {"start": v(23.55, 72.47) * mm, "mid": v(25.4, 74.45) * mm, "end": v(27.51, 76.14) * mm});
            skArc(sketch, "E13.28.3", {"start": v(28.2, 76.25) * mm, "mid": v(27.85, 76.28) * mm, "end": v(27.51, 76.14) * mm});
            skLineSegment(sketch, "E13.28.4", {"start": v(28.2, 76.25) * mm, "end": v(29.15, 75.94) * mm});
            skLineSegment(sketch, "E13.28.5", {"start": v(30.06, 75.53) * mm, "end": v(29.15, 75.94) * mm});
            skArc(sketch, "E13.28.6", {"start": v(30.5, 75) * mm, "mid": v(30.34, 75.32) * mm, "end": v(30.06, 75.53) * mm});
            skArc(sketch, "E13.28.7", {"start": v(31, 69.61) * mm, "mid": v(30.94, 72.32) * mm, "end": v(30.5, 75) * mm});
            skLineSegment(sketch, "E13.28.8", {"start": v(31, 69.61) * mm, "end": v(29.44, 65.55) * mm});
            skArc(sketch, "E13.28.9", {"start": v(29.44, 65.55) * mm, "mid": v(29.44, 64.98) * mm, "end": v(29.84, 64.56) * mm});
            skArc(sketch, "E13.29.0", {"start": v(6.44, 70.83) * mm, "mid": v(7, 71) * mm, "end": v(7.29, 71.49) * mm});
            skLineSegment(sketch, "E13.29.1", {"start": v(7.97, 75.78) * mm, "end": v(7.29, 71.49) * mm});
            skArc(sketch, "E13.29.2", {"start": v(7.97, 75.78) * mm, "mid": v(9.37, 78.1) * mm, "end": v(11.08, 80.2) * mm});
            skArc(sketch, "E13.29.3", {"start": v(11.74, 80.44) * mm, "mid": v(11.38, 80.4) * mm, "end": v(11.08, 80.2) * mm});
            skLineSegment(sketch, "E13.29.4", {"start": v(11.74, 80.44) * mm, "end": v(12.72, 80.34) * mm});
            skLineSegment(sketch, "E13.29.5", {"start": v(13.7, 80.13) * mm, "end": v(12.72, 80.34) * mm});
            skArc(sketch, "E13.29.6", {"start": v(14.24, 79.7) * mm, "mid": v(14.02, 79.98) * mm, "end": v(13.7, 80.13) * mm});
            skArc(sketch, "E13.29.7", {"start": v(15.84, 74.53) * mm, "mid": v(15.23, 77.17) * mm, "end": v(14.24, 79.7) * mm});
            skLineSegment(sketch, "E13.29.8", {"start": v(15.84, 74.53) * mm, "end": v(15.16, 70.24) * mm});
            skArc(sketch, "E13.29.9", {"start": v(15.16, 70.24) * mm, "mid": v(15.29, 69.68) * mm, "end": v(15.77, 69.35) * mm});
            skArc(sketch, "E14.trimOffspring", {"start": v(6.44, 70.83) * mm, "mid": v(3.72, 71.02) * mm, "end": v(1, 71.11) * mm});
            skArc(sketch, "E15.trimOffspring", {"start": v(21.02, 67.94) * mm, "mid": v(18.4, 68.7) * mm, "end": v(15.77, 69.35) * mm});
            skArc(sketch, "E16.trimOffspring", {"start": v(34.69, 62.09) * mm, "mid": v(32.29, 63.37) * mm, "end": v(29.84, 64.56) * mm});
            skArc(sketch, "E17.trimOffspring", {"start": v(46.84, 53.52) * mm, "mid": v(44.76, 55.27) * mm, "end": v(42.61, 56.94) * mm});
            skArc(sketch, "E18.trimOffspring", {"start": v(56.94, 42.61) * mm, "mid": v(55.27, 44.76) * mm, "end": v(53.52, 46.84) * mm});
            skArc(sketch, "E19.trimOffspring", {"start": v(64.56, 29.84) * mm, "mid": v(63.37, 32.29) * mm, "end": v(62.09, 34.69) * mm});
            skArc(sketch, "E20.trimOffspring", {"start": v(69.35, 15.77) * mm, "mid": v(68.7, 18.4) * mm, "end": v(67.94, 21.02) * mm});
            skArc(sketch, "E21.trimOffspring", {"start": v(71.11, 1) * mm, "mid": v(71.02, 3.72) * mm, "end": v(70.83, 6.44) * mm});
            skArc(sketch, "E22.trimOffspring", {"start": v(69.77, -13.8) * mm, "mid": v(70.24, -11.13) * mm, "end": v(70.62, -8.43) * mm});
            skArc(sketch, "E23.trimOffspring", {"start": v(65.37, -28) * mm, "mid": v(66.4, -25.49) * mm, "end": v(67.32, -22.93) * mm});
            skArc(sketch, "E24.trimOffspring", {"start": v(58.12, -40.99) * mm, "mid": v(59.65, -38.73) * mm, "end": v(61.08, -36.42) * mm});
            skArc(sketch, "E25.trimOffspring", {"start": v(48.33, -52.18) * mm, "mid": v(50.29, -50.29) * mm, "end": v(52.18, -48.33) * mm});
            skArc(sketch, "E26.trimOffspring", {"start": v(36.42, -61.08) * mm, "mid": v(38.73, -59.65) * mm, "end": v(40.99, -58.12) * mm});
            skArc(sketch, "E27.trimOffspring", {"start": v(22.93, -67.32) * mm, "mid": v(25.49, -66.4) * mm, "end": v(28, -65.37) * mm});
            skArc(sketch, "E28.trimOffspring", {"start": v(8.43, -70.62) * mm, "mid": v(11.13, -70.24) * mm, "end": v(13.8, -69.77) * mm});
            skArc(sketch, "E29.trimOffspring", {"start": v(-6.44, -70.83) * mm, "mid": v(-3.72, -71.02) * mm, "end": v(-1, -71.11) * mm});
            skArc(sketch, "E30.trimOffspring", {"start": v(-21.02, -67.94) * mm, "mid": v(-18.4, -68.7) * mm, "end": v(-15.77, -69.35) * mm});
            skArc(sketch, "E31.trimOffspring", {"start": v(-34.69, -62.09) * mm, "mid": v(-32.29, -63.37) * mm, "end": v(-29.84, -64.56) * mm});
            skArc(sketch, "E32.trimOffspring", {"start": v(-46.84, -53.52) * mm, "mid": v(-44.76, -55.27) * mm, "end": v(-42.61, -56.94) * mm});
            skArc(sketch, "E33.trimOffspring", {"start": v(-56.94, -42.61) * mm, "mid": v(-55.27, -44.76) * mm, "end": v(-53.52, -46.84) * mm});
            skArc(sketch, "E34.trimOffspring", {"start": v(-64.56, -29.84) * mm, "mid": v(-63.37, -32.29) * mm, "end": v(-62.09, -34.69) * mm});
            skArc(sketch, "E35.trimOffspring", {"start": v(-69.35, -15.77) * mm, "mid": v(-68.7, -18.4) * mm, "end": v(-67.94, -21.02) * mm});
            skArc(sketch, "E36.trimOffspring", {"start": v(-71.11, -1) * mm, "mid": v(-71.02, -3.72) * mm, "end": v(-70.83, -6.44) * mm});
            skArc(sketch, "E37.trimOffspring", {"start": v(-69.77, 13.8) * mm, "mid": v(-70.24, 11.13) * mm, "end": v(-70.62, 8.43) * mm});
            skArc(sketch, "E38.trimOffspring", {"start": v(-65.37, 28) * mm, "mid": v(-66.4, 25.49) * mm, "end": v(-67.32, 22.93) * mm});
            skArc(sketch, "E39.trimOffspring", {"start": v(-58.12, 40.99) * mm, "mid": v(-59.65, 38.73) * mm, "end": v(-61.08, 36.42) * mm});
            skArc(sketch, "E40.trimOffspring", {"start": v(-48.33, 52.18) * mm, "mid": v(-50.29, 50.29) * mm, "end": v(-52.18, 48.33) * mm});
            skArc(sketch, "E41.trimOffspring", {"start": v(-36.42, 61.08) * mm, "mid": v(-38.73, 59.65) * mm, "end": v(-40.99, 58.12) * mm});
            skArc(sketch, "E42.trimOffspring", {"start": v(-22.93, 67.32) * mm, "mid": v(-25.49, 66.4) * mm, "end": v(-28, 65.37) * mm});
            skArc(sketch, "E43", {"start": v(-4.76, 65.45) * mm, "mid": v(-6.1, 65.34) * mm, "end": v(-7.42, 65.2) * mm});
            skLineSegment(sketch, "E44.MirrorCS", {"start": v(-3.86, 62.97) * mm, "end": v(-3.92, 64.69) * mm});
            skArc(sketch, "E45.MirrorCS", {"start": v(-3.86, 62.97) * mm, "mid": v(-3.4, 61.88) * mm, "end": v(-2.86, 60.84) * mm});
            skLineSegment(sketch, "E46.MirrorCS", {"start": v(-2.17, 60.44) * mm, "end": v(-1.79, 60.44) * mm});
            skLineSegment(sketch, "E47.MirrorCS", {"start": v(-1.4, 60.46) * mm, "end": v(-1.79, 60.44) * mm});
            skArc(sketch, "E48.MirrorCS", {"start": v(0.12, 63.1) * mm, "mid": v(-0.27, 61.98) * mm, "end": v(-0.75, 60.9) * mm});
            skLineSegment(sketch, "E49.MirrorCS", {"start": v(0.12, 63.1) * mm, "end": v(0.07, 64.81) * mm});
            skPoint(sketch, "E50.visualSharp", {"position": v(-3.94, 65.5) * mm});
            skArc(sketch, "E50.filletArc", {"start": v(-3.92, 64.69) * mm, "mid": v(-4.18, 65.25) * mm, "end": v(-4.76, 65.45) * mm});
            skPoint(sketch, "E51.visualSharp", {"position": v(0.04, 65.63) * mm});
            skArc(sketch, "E51.filletArc", {"start": v(0.87, 65.63) * mm, "mid": v(0.3, 65.39) * mm, "end": v(0.07, 64.81) * mm});
            skPoint(sketch, "E52.visualSharp", {"position": v(-0.96, 60.5) * mm});
            skArc(sketch, "E52.filletArc", {"start": v(-1.4, 60.46) * mm, "mid": v(-1.02, 60.6) * mm, "end": v(-0.75, 60.9) * mm});
            skPoint(sketch, "E53.visualSharp", {"position": v(-2.62, 60.44) * mm});
            skArc(sketch, "E53.filletArc", {"start": v(-2.86, 60.84) * mm, "mid": v(-2.57, 60.55) * mm, "end": v(-2.17, 60.44) * mm});
            skArc(sketch, "E54.1.0", {"start": v(-12.04, 63.67) * mm, "mid": v(-12.37, 64.2) * mm, "end": v(-12.98, 64.32) * mm});
            skLineSegment(sketch, "E54.1.1", {"start": v(-11.78, 61.97) * mm, "end": v(-12.04, 63.67) * mm});
            skArc(sketch, "E54.1.2", {"start": v(-11.78, 61.97) * mm, "mid": v(-11.18, 60.95) * mm, "end": v(-10.51, 59.98) * mm});
            skArc(sketch, "E54.1.3", {"start": v(-10.51, 59.98) * mm, "mid": v(-10.19, 59.73) * mm, "end": v(-9.78, 59.67) * mm});
            skLineSegment(sketch, "E54.1.4", {"start": v(-9.78, 59.67) * mm, "end": v(-9.4, 59.72) * mm});
            skLineSegment(sketch, "E54.1.5", {"start": v(-9.02, 59.8) * mm, "end": v(-9.4, 59.72) * mm});
            skArc(sketch, "E54.1.6", {"start": v(-9.02, 59.8) * mm, "mid": v(-8.65, 59.97) * mm, "end": v(-8.42, 60.31) * mm});
            skLineSegment(sketch, "E54.1.7", {"start": v(-7.84, 62.6) * mm, "end": v(-8.1, 64.3) * mm});
            skArc(sketch, "E54.1.8", {"start": v(-7.84, 62.6) * mm, "mid": v(-8.09, 61.44) * mm, "end": v(-8.42, 60.31) * mm});
            skArc(sketch, "E54.1.9", {"start": v(-7.42, 65.2) * mm, "mid": v(-7.95, 64.9) * mm, "end": v(-8.1, 64.3) * mm});
            skArc(sketch, "E54.2.0", {"start": v(-19.98, 61.64) * mm, "mid": v(-20.37, 62.12) * mm, "end": v(-20.99, 62.16) * mm});
            skLineSegment(sketch, "E54.2.1", {"start": v(-19.5, 59.98) * mm, "end": v(-19.98, 61.64) * mm});
            skArc(sketch, "E54.2.2", {"start": v(-19.5, 59.98) * mm, "mid": v(-18.78, 59.05) * mm, "end": v(-18, 58.17) * mm});
            skArc(sketch, "E54.2.3", {"start": v(-18, 58.17) * mm, "mid": v(-17.64, 57.96) * mm, "end": v(-17.23, 57.96) * mm});
            skLineSegment(sketch, "E54.2.4", {"start": v(-17.23, 57.96) * mm, "end": v(-16.86, 58.05) * mm});
            skLineSegment(sketch, "E54.2.5", {"start": v(-16.5, 58.17) * mm, "end": v(-16.86, 58.05) * mm});
            skArc(sketch, "E54.2.6", {"start": v(-16.5, 58.17) * mm, "mid": v(-16.15, 58.4) * mm, "end": v(-15.97, 58.76) * mm});
            skLineSegment(sketch, "E54.2.7", {"start": v(-15.67, 61.1) * mm, "end": v(-16.15, 62.75) * mm});
            skArc(sketch, "E54.2.8", {"start": v(-15.67, 61.1) * mm, "mid": v(-15.77, 59.92) * mm, "end": v(-15.97, 58.76) * mm});
            skArc(sketch, "E54.2.9", {"start": v(-15.58, 63.74) * mm, "mid": v(-16.07, 63.36) * mm, "end": v(-16.15, 62.75) * mm});
            skArc(sketch, "E54.3.0", {"start": v(-27.6, 58.63) * mm, "mid": v(-28.05, 59.05) * mm, "end": v(-28.66, 59.02) * mm});
            skLineSegment(sketch, "E54.3.1", {"start": v(-26.91, 57.05) * mm, "end": v(-27.6, 58.63) * mm});
            skArc(sketch, "E54.3.2", {"start": v(-26.91, 57.05) * mm, "mid": v(-26.08, 56.21) * mm, "end": v(-25.2, 55.44) * mm});
            skArc(sketch, "E54.3.3", {"start": v(-25.2, 55.44) * mm, "mid": v(-24.82, 55.27) * mm, "end": v(-24.41, 55.32) * mm});
            skLineSegment(sketch, "E54.3.4", {"start": v(-24.41, 55.32) * mm, "end": v(-24.05, 55.46) * mm});
            skLineSegment(sketch, "E54.3.5", {"start": v(-23.7, 55.62) * mm, "end": v(-24.05, 55.46) * mm});
            skArc(sketch, "E54.3.6", {"start": v(-23.7, 55.62) * mm, "mid": v(-23.4, 55.9) * mm, "end": v(-23.26, 56.28) * mm});
            skLineSegment(sketch, "E54.3.7", {"start": v(-23.25, 58.63) * mm, "end": v(-23.94, 60.21) * mm});
            skArc(sketch, "E54.3.8", {"start": v(-23.25, 58.63) * mm, "mid": v(-23.21, 57.45) * mm, "end": v(-23.26, 56.28) * mm});
            skArc(sketch, "E54.3.9", {"start": v(-23.5, 61.26) * mm, "mid": v(-23.94, 60.83) * mm, "end": v(-23.94, 60.21) * mm});
            skArc(sketch, "E54.4.0", {"start": v(-34.78, 54.69) * mm, "mid": v(-35.28, 55.05) * mm, "end": v(-35.89, 54.95) * mm});
            skLineSegment(sketch, "E54.4.1", {"start": v(-33.9, 53.2) * mm, "end": v(-34.78, 54.69) * mm});
            skArc(sketch, "E54.4.2", {"start": v(-33.9, 53.2) * mm, "mid": v(-32.97, 52.48) * mm, "end": v(-32, 51.83) * mm});
            skArc(sketch, "E54.4.3", {"start": v(-32, 51.83) * mm, "mid": v(-31.6, 51.7) * mm, "end": v(-31.2, 51.8) * mm});
            skLineSegment(sketch, "E54.4.4", {"start": v(-31.2, 51.8) * mm, "end": v(-30.87, 52) * mm});
            skLineSegment(sketch, "E54.4.5", {"start": v(-30.54, 52.2) * mm, "end": v(-30.87, 52) * mm});
            skArc(sketch, "E54.4.6", {"start": v(-30.54, 52.2) * mm, "mid": v(-30.26, 52.5) * mm, "end": v(-30.18, 52.9) * mm});
            skLineSegment(sketch, "E54.4.7", {"start": v(-30.47, 55.24) * mm, "end": v(-31.35, 56.72) * mm});
            skArc(sketch, "E54.4.8", {"start": v(-30.47, 55.24) * mm, "mid": v(-30.28, 54.07) * mm, "end": v(-30.18, 52.9) * mm});
            skArc(sketch, "E54.4.9", {"start": v(-31.04, 57.81) * mm, "mid": v(-31.43, 57.33) * mm, "end": v(-31.35, 56.72) * mm});
            skArc(sketch, "E54.5.0", {"start": v(-41.4, 49.88) * mm, "mid": v(-41.95, 50.18) * mm, "end": v(-42.54, 50) * mm});
            skLineSegment(sketch, "E54.5.1", {"start": v(-40.35, 48.52) * mm, "end": v(-41.4, 49.88) * mm});
            skArc(sketch, "E54.5.2", {"start": v(-40.35, 48.52) * mm, "mid": v(-39.34, 47.91) * mm, "end": v(-38.29, 47.39) * mm});
            skArc(sketch, "E54.5.3", {"start": v(-38.29, 47.39) * mm, "mid": v(-37.88, 47.32) * mm, "end": v(-37.5, 47.47) * mm});
            skLineSegment(sketch, "E54.5.4", {"start": v(-37.5, 47.47) * mm, "end": v(-37.19, 47.7) * mm});
            skLineSegment(sketch, "E54.5.5", {"start": v(-36.9, 47.94) * mm, "end": v(-37.19, 47.7) * mm});
            skArc(sketch, "E54.5.6", {"start": v(-36.9, 47.94) * mm, "mid": v(-36.66, 48.27) * mm, "end": v(-36.62, 48.68) * mm});
            skLineSegment(sketch, "E54.5.7", {"start": v(-37.2, 50.96) * mm, "end": v(-38.26, 52.32) * mm});
            skArc(sketch, "E54.5.8", {"start": v(-37.2, 50.96) * mm, "mid": v(-36.87, 49.83) * mm, "end": v(-36.62, 48.68) * mm});
            skArc(sketch, "E54.5.9", {"start": v(-38.1, 53.45) * mm, "mid": v(-38.41, 52.92) * mm, "end": v(-38.26, 52.32) * mm});
            skArc(sketch, "E54.6.0", {"start": v(-47.39, 44.28) * mm, "mid": v(-47.96, 44.5) * mm, "end": v(-48.52, 44.25) * mm});
            skLineSegment(sketch, "E54.6.1", {"start": v(-46.17, 43.06) * mm, "end": v(-47.39, 44.28) * mm});
            skArc(sketch, "E54.6.2", {"start": v(-46.17, 43.06) * mm, "mid": v(-45.09, 42.59) * mm, "end": v(-43.98, 42.2) * mm});
            skArc(sketch, "E54.6.3", {"start": v(-43.98, 42.2) * mm, "mid": v(-43.57, 42.18) * mm, "end": v(-43.2, 42.37) * mm});
            skLineSegment(sketch, "E54.6.4", {"start": v(-43.2, 42.37) * mm, "end": v(-42.92, 42.64) * mm});
            skLineSegment(sketch, "E54.6.5", {"start": v(-42.66, 42.92) * mm, "end": v(-42.92, 42.64) * mm});
            skArc(sketch, "E54.6.6", {"start": v(-42.66, 42.92) * mm, "mid": v(-42.47, 43.28) * mm, "end": v(-42.48, 43.69) * mm});
            skLineSegment(sketch, "E54.6.7", {"start": v(-43.35, 45.88) * mm, "end": v(-44.56, 47.1) * mm});
            skArc(sketch, "E54.6.8", {"start": v(-43.35, 45.88) * mm, "mid": v(-42.87, 44.8) * mm, "end": v(-42.48, 43.69) * mm});
            skArc(sketch, "E54.6.9", {"start": v(-44.54, 48.24) * mm, "mid": v(-44.8, 47.67) * mm, "end": v(-44.56, 47.1) * mm});
            skArc(sketch, "E54.7.0", {"start": v(-52.61, 37.97) * mm, "mid": v(-53.2, 38.13) * mm, "end": v(-53.74, 37.8) * mm});
            skLineSegment(sketch, "E54.7.1", {"start": v(-51.25, 36.92) * mm, "end": v(-52.61, 37.97) * mm});
            skArc(sketch, "E54.7.2", {"start": v(-51.25, 36.92) * mm, "mid": v(-50.12, 36.58) * mm, "end": v(-48.97, 36.33) * mm});
            skArc(sketch, "E54.7.3", {"start": v(-48.97, 36.33) * mm, "mid": v(-48.56, 36.37) * mm, "end": v(-48.22, 36.6) * mm});
            skLineSegment(sketch, "E54.7.4", {"start": v(-48.22, 36.6) * mm, "end": v(-47.98, 36.9) * mm});
            skLineSegment(sketch, "E54.7.5", {"start": v(-47.75, 37.21) * mm, "end": v(-47.98, 36.9) * mm});
            skArc(sketch, "E54.7.6", {"start": v(-47.75, 37.21) * mm, "mid": v(-47.6, 37.6) * mm, "end": v(-47.67, 38) * mm});
            skLineSegment(sketch, "E54.7.7", {"start": v(-48.8, 40.07) * mm, "end": v(-50.17, 41.12) * mm});
            skArc(sketch, "E54.7.8", {"start": v(-48.8, 40.07) * mm, "mid": v(-48.2, 39.06) * mm, "end": v(-47.67, 38) * mm});
            skArc(sketch, "E54.7.9", {"start": v(-50.28, 42.25) * mm, "mid": v(-50.47, 41.66) * mm, "end": v(-50.17, 41.12) * mm});
            skArc(sketch, "E54.8.0", {"start": v(-57, 31.06) * mm, "mid": v(-57.62, 31.14) * mm, "end": v(-58.1, 30.75) * mm});
            skLineSegment(sketch, "E54.8.1", {"start": v(-55.52, 30.18) * mm, "end": v(-57, 31.06) * mm});
            skArc(sketch, "E54.8.2", {"start": v(-55.52, 30.18) * mm, "mid": v(-54.36, 30) * mm, "end": v(-53.19, 29.9) * mm});
            skArc(sketch, "E54.8.3", {"start": v(-53.19, 29.9) * mm, "mid": v(-52.79, 29.98) * mm, "end": v(-52.48, 30.25) * mm});
            skLineSegment(sketch, "E54.8.4", {"start": v(-52.48, 30.25) * mm, "end": v(-52.28, 30.58) * mm});
            skLineSegment(sketch, "E54.8.5", {"start": v(-52.1, 30.92) * mm, "end": v(-52.28, 30.58) * mm});
            skArc(sketch, "E54.8.6", {"start": v(-52.1, 30.92) * mm, "mid": v(-52, 31.31) * mm, "end": v(-52.11, 31.7) * mm});
            skLineSegment(sketch, "E54.8.7", {"start": v(-53.5, 33.62) * mm, "end": v(-54.98, 34.5) * mm});
            skArc(sketch, "E54.8.8", {"start": v(-53.5, 33.62) * mm, "mid": v(-52.77, 32.69) * mm, "end": v(-52.11, 31.7) * mm});
            skArc(sketch, "E54.8.9", {"start": v(-55.23, 35.6) * mm, "mid": v(-55.34, 35) * mm, "end": v(-54.98, 34.5) * mm});
            skArc(sketch, "E54.9.0", {"start": v(-60.5, 23.65) * mm, "mid": v(-61.12, 23.65) * mm, "end": v(-61.55, 23.2) * mm});
            skLineSegment(sketch, "E54.9.1", {"start": v(-58.92, 22.97) * mm, "end": v(-60.5, 23.65) * mm});
            skArc(sketch, "E54.9.2", {"start": v(-58.92, 22.97) * mm, "mid": v(-57.74, 22.92) * mm, "end": v(-56.56, 22.97) * mm});
            skArc(sketch, "E54.9.3", {"start": v(-56.56, 22.97) * mm, "mid": v(-56.18, 23.1) * mm, "end": v(-55.91, 23.42) * mm});
            skLineSegment(sketch, "E54.9.4", {"start": v(-55.91, 23.42) * mm, "end": v(-55.75, 23.77) * mm});
            skLineSegment(sketch, "E54.9.5", {"start": v(-55.6, 24.12) * mm, "end": v(-55.75, 23.77) * mm});
            skArc(sketch, "E54.9.6", {"start": v(-55.6, 24.12) * mm, "mid": v(-55.56, 24.53) * mm, "end": v(-55.73, 24.9) * mm});
            skLineSegment(sketch, "E54.9.7", {"start": v(-57.33, 26.63) * mm, "end": v(-58.92, 27.31) * mm});
            skArc(sketch, "E54.9.8", {"start": v(-57.33, 26.63) * mm, "mid": v(-56.5, 25.8) * mm, "end": v(-55.73, 24.9) * mm});
            skArc(sketch, "E54.9.9", {"start": v(-59.31, 28.38) * mm, "mid": v(-59.34, 27.76) * mm, "end": v(-58.92, 27.31) * mm});
            skArc(sketch, "E54.10.0", {"start": v(-63.04, 15.86) * mm, "mid": v(-63.65, 15.79) * mm, "end": v(-64.02, 15.3) * mm});
            skLineSegment(sketch, "E54.10.1", {"start": v(-61.38, 15.38) * mm, "end": v(-63.04, 15.86) * mm});
            skArc(sketch, "E54.10.2", {"start": v(-61.38, 15.38) * mm, "mid": v(-60.21, 15.49) * mm, "end": v(-59.05, 15.68) * mm});
            skArc(sketch, "E54.10.3", {"start": v(-59.05, 15.68) * mm, "mid": v(-58.68, 15.86) * mm, "end": v(-58.46, 16.2) * mm});
            skLineSegment(sketch, "E54.10.4", {"start": v(-58.46, 16.2) * mm, "end": v(-58.34, 16.57) * mm});
            skLineSegment(sketch, "E54.10.5", {"start": v(-58.24, 16.95) * mm, "end": v(-58.34, 16.57) * mm});
            skArc(sketch, "E54.10.6", {"start": v(-58.24, 16.95) * mm, "mid": v(-58.25, 17.36) * mm, "end": v(-58.46, 17.7) * mm});
            skLineSegment(sketch, "E54.10.7", {"start": v(-60.27, 19.21) * mm, "end": v(-61.92, 19.7) * mm});
            skArc(sketch, "E54.10.8", {"start": v(-60.27, 19.21) * mm, "mid": v(-59.34, 18.5) * mm, "end": v(-58.46, 17.7) * mm});
            skArc(sketch, "E54.10.9", {"start": v(-62.45, 20.7) * mm, "mid": v(-62.4, 20.08) * mm, "end": v(-61.92, 19.7) * mm});
            skArc(sketch, "E54.11.0", {"start": v(-64.58, 7.82) * mm, "mid": v(-65.18, 7.67) * mm, "end": v(-65.48, 7.13) * mm});
            skLineSegment(sketch, "E54.11.1", {"start": v(-62.88, 7.55) * mm, "end": v(-64.58, 7.82) * mm});
            skArc(sketch, "E54.11.2", {"start": v(-62.88, 7.55) * mm, "mid": v(-61.73, 7.8) * mm, "end": v(-60.6, 8.14) * mm});
            skArc(sketch, "E54.11.3", {"start": v(-60.6, 8.14) * mm, "mid": v(-60.26, 8.37) * mm, "end": v(-60.08, 8.74) * mm});
            skLineSegment(sketch, "E54.11.4", {"start": v(-60.08, 8.74) * mm, "end": v(-60, 9.11) * mm});
            skLineSegment(sketch, "E54.11.5", {"start": v(-59.96, 9.5) * mm, "end": v(-60, 9.11) * mm});
            skArc(sketch, "E54.11.6", {"start": v(-59.96, 9.5) * mm, "mid": v(-60.01, 9.9) * mm, "end": v(-60.27, 10.22) * mm});
            skLineSegment(sketch, "E54.11.7", {"start": v(-62.25, 11.49) * mm, "end": v(-63.95, 11.76) * mm});
            skArc(sketch, "E54.11.8", {"start": v(-62.25, 11.49) * mm, "mid": v(-61.24, 10.9) * mm, "end": v(-60.27, 10.22) * mm});
            skArc(sketch, "E54.11.9", {"start": v(-64.6, 12.7) * mm, "mid": v(-64.48, 12.09) * mm, "end": v(-63.95, 11.76) * mm});
            skArc(sketch, "E54.12.0", {"start": v(-65.1, -0.36) * mm, "mid": v(-65.68, -0.58) * mm, "end": v(-65.91, -1.15) * mm});
            skLineSegment(sketch, "E54.12.1", {"start": v(-63.38, -0.41) * mm, "end": v(-65.1, -0.36) * mm});
            skArc(sketch, "E54.12.2", {"start": v(-63.38, -0.41) * mm, "mid": v(-62.27, -0.02) * mm, "end": v(-61.2, 0.46) * mm});
            skArc(sketch, "E54.12.3", {"start": v(-61.2, 0.46) * mm, "mid": v(-60.88, 0.73) * mm, "end": v(-60.75, 1.12) * mm});
            skLineSegment(sketch, "E54.12.4", {"start": v(-60.75, 1.12) * mm, "end": v(-60.72, 1.5) * mm});
            skLineSegment(sketch, "E54.12.5", {"start": v(-60.72, 1.89) * mm, "end": v(-60.72, 1.5) * mm});
            skArc(sketch, "E54.12.6", {"start": v(-60.72, 1.89) * mm, "mid": v(-60.83, 2.28) * mm, "end": v(-61.12, 2.57) * mm});
            skLineSegment(sketch, "E54.12.7", {"start": v(-63.25, 3.58) * mm, "end": v(-64.97, 3.63) * mm});
            skArc(sketch, "E54.12.8", {"start": v(-63.25, 3.58) * mm, "mid": v(-62.17, 3.11) * mm, "end": v(-61.12, 2.57) * mm});
            skArc(sketch, "E54.12.9", {"start": v(-65.74, 4.48) * mm, "mid": v(-65.54, 3.9) * mm, "end": v(-64.97, 3.63) * mm});
            skArc(sketch, "E54.13.0", {"start": v(-64.6, -8.53) * mm, "mid": v(-65.14, -8.83) * mm, "end": v(-65.3, -9.42) * mm});
            skLineSegment(sketch, "E54.13.1", {"start": v(-62.88, -8.37) * mm, "end": v(-64.6, -8.53) * mm});
            skArc(sketch, "E54.13.2", {"start": v(-62.88, -8.37) * mm, "mid": v(-61.83, -7.84) * mm, "end": v(-60.82, -7.23) * mm});
            skArc(sketch, "E54.13.3", {"start": v(-60.82, -7.23) * mm, "mid": v(-60.54, -6.93) * mm, "end": v(-60.46, -6.52) * mm});
            skLineSegment(sketch, "E54.13.4", {"start": v(-60.46, -6.52) * mm, "end": v(-60.48, -6.14) * mm});
            skLineSegment(sketch, "E54.13.5", {"start": v(-60.53, -5.76) * mm, "end": v(-60.48, -6.14) * mm});
            skArc(sketch, "E54.13.6", {"start": v(-60.53, -5.76) * mm, "mid": v(-60.69, -5.38) * mm, "end": v(-61.01, -5.13) * mm});
            skLineSegment(sketch, "E54.13.7", {"start": v(-63.25, -4.4) * mm, "end": v(-64.97, -4.56) * mm});
            skArc(sketch, "E54.13.8", {"start": v(-63.25, -4.4) * mm, "mid": v(-62.12, -4.72) * mm, "end": v(-61.01, -5.13) * mm});
            skArc(sketch, "E54.13.9", {"start": v(-65.83, -3.82) * mm, "mid": v(-65.56, -4.37) * mm, "end": v(-64.97, -4.56) * mm});
            skArc(sketch, "E54.14.0", {"start": v(-63.06, -16.58) * mm, "mid": v(-63.57, -16.94) * mm, "end": v(-63.65, -17.55) * mm});
            skLineSegment(sketch, "E54.14.1", {"start": v(-61.38, -16.2) * mm, "end": v(-63.06, -16.58) * mm});
            skArc(sketch, "E54.14.2", {"start": v(-61.38, -16.2) * mm, "mid": v(-60.4, -15.54) * mm, "end": v(-59.48, -14.82) * mm});
            skArc(sketch, "E54.14.3", {"start": v(-59.48, -14.82) * mm, "mid": v(-59.25, -14.48) * mm, "end": v(-59.22, -14.07) * mm});
            skLineSegment(sketch, "E54.14.4", {"start": v(-59.22, -14.07) * mm, "end": v(-59.29, -13.7) * mm});
            skLineSegment(sketch, "E54.14.5", {"start": v(-59.38, -13.32) * mm, "end": v(-59.29, -13.7) * mm});
            skArc(sketch, "E54.14.6", {"start": v(-59.38, -13.32) * mm, "mid": v(-59.59, -12.96) * mm, "end": v(-59.94, -12.75) * mm});
            skLineSegment(sketch, "E54.14.7", {"start": v(-62.25, -12.3) * mm, "end": v(-63.93, -12.69) * mm});
            skArc(sketch, "E54.14.8", {"start": v(-62.25, -12.3) * mm, "mid": v(-61.09, -12.49) * mm, "end": v(-59.94, -12.75) * mm});
            skArc(sketch, "E54.14.9", {"start": v(-64.88, -12.06) * mm, "mid": v(-64.54, -12.57) * mm, "end": v(-63.93, -12.69) * mm});
            skArc(sketch, "E54.15.0", {"start": v(-60.54, -24.37) * mm, "mid": v(-61, -24.8) * mm, "end": v(-61, -25.4) * mm});
            skLineSegment(sketch, "E54.15.1", {"start": v(-58.92, -23.79) * mm, "end": v(-60.54, -24.37) * mm});
            skArc(sketch, "E54.15.2", {"start": v(-58.92, -23.79) * mm, "mid": v(-58.03, -23.01) * mm, "end": v(-57.2, -22.17) * mm});
            skArc(sketch, "E54.15.3", {"start": v(-57.2, -22.17) * mm, "mid": v(-57.02, -21.8) * mm, "end": v(-57.04, -21.4) * mm});
            skLineSegment(sketch, "E54.15.4", {"start": v(-57.04, -21.4) * mm, "end": v(-57.16, -21.03) * mm});
            skLineSegment(sketch, "E54.15.5", {"start": v(-57.3, -20.68) * mm, "end": v(-57.16, -21.03) * mm});
            skArc(sketch, "E54.15.6", {"start": v(-57.3, -20.68) * mm, "mid": v(-57.54, -20.35) * mm, "end": v(-57.92, -20.19) * mm});
            skLineSegment(sketch, "E54.15.7", {"start": v(-60.27, -20.03) * mm, "end": v(-61.9, -20.62) * mm});
            skArc(sketch, "E54.15.8", {"start": v(-60.27, -20.03) * mm, "mid": v(-59.1, -20.07) * mm, "end": v(-57.92, -20.19) * mm});
            skArc(sketch, "E54.15.9", {"start": v(-62.9, -20.11) * mm, "mid": v(-62.5, -20.58) * mm, "end": v(-61.9, -20.62) * mm});
            skArc(sketch, "E54.16.0", {"start": v(-57.06, -31.78) * mm, "mid": v(-57.45, -32.26) * mm, "end": v(-57.39, -32.87) * mm});
            skLineSegment(sketch, "E54.16.1", {"start": v(-55.52, -31) * mm, "end": v(-57.06, -31.78) * mm});
            skArc(sketch, "E54.16.2", {"start": v(-55.52, -31) * mm, "mid": v(-54.74, -30.12) * mm, "end": v(-54.03, -29.19) * mm});
            skArc(sketch, "E54.16.3", {"start": v(-54.03, -29.19) * mm, "mid": v(-53.88, -28.8) * mm, "end": v(-53.96, -28.4) * mm});
            skLineSegment(sketch, "E54.16.4", {"start": v(-53.96, -28.4) * mm, "end": v(-54.12, -28.05) * mm});
            skLineSegment(sketch, "E54.16.5", {"start": v(-54.3, -27.71) * mm, "end": v(-54.12, -28.05) * mm});
            skArc(sketch, "E54.16.6", {"start": v(-54.3, -27.71) * mm, "mid": v(-54.59, -27.42) * mm, "end": v(-54.98, -27.3) * mm});
            skLineSegment(sketch, "E54.16.7", {"start": v(-57.33, -27.45) * mm, "end": v(-58.87, -28.23) * mm});
            skArc(sketch, "E54.16.8", {"start": v(-57.33, -27.45) * mm, "mid": v(-56.16, -27.33) * mm, "end": v(-54.98, -27.3) * mm});
            skArc(sketch, "E54.16.9", {"start": v(-59.94, -27.86) * mm, "mid": v(-59.49, -28.27) * mm, "end": v(-58.87, -28.23) * mm});
            skArc(sketch, "E54.17.0", {"start": v(-52.68, -38.7) * mm, "mid": v(-53, -39.22) * mm, "end": v(-52.86, -39.83) * mm});
            skLineSegment(sketch, "E54.17.1", {"start": v(-51.25, -37.74) * mm, "end": v(-52.68, -38.7) * mm});
            skArc(sketch, "E54.17.2", {"start": v(-51.25, -37.74) * mm, "mid": v(-50.58, -36.76) * mm, "end": v(-50, -35.75) * mm});
            skArc(sketch, "E54.17.3", {"start": v(-50, -35.75) * mm, "mid": v(-49.9, -35.35) * mm, "end": v(-50.02, -34.95) * mm});
            skLineSegment(sketch, "E54.17.4", {"start": v(-50.02, -34.95) * mm, "end": v(-50.23, -34.63) * mm});
            skLineSegment(sketch, "E54.17.5", {"start": v(-50.45, -34.32) * mm, "end": v(-50.23, -34.63) * mm});
            skArc(sketch, "E54.17.6", {"start": v(-50.45, -34.32) * mm, "mid": v(-50.77, -34.06) * mm, "end": v(-51.18, -34) * mm});
            skLineSegment(sketch, "E54.17.7", {"start": v(-53.5, -34.44) * mm, "end": v(-54.92, -35.4) * mm});
            skArc(sketch, "E54.17.8", {"start": v(-53.5, -34.44) * mm, "mid": v(-52.34, -34.18) * mm, "end": v(-51.18, -34) * mm});
            skArc(sketch, "E54.17.9", {"start": v(-56.03, -35.17) * mm, "mid": v(-55.52, -35.52) * mm, "end": v(-54.92, -35.4) * mm});
            skArc(sketch, "E54.18.0", {"start": v(-47.46, -45.02) * mm, "mid": v(-47.73, -45.58) * mm, "end": v(-47.5, -46.16) * mm});
            skLineSegment(sketch, "E54.18.1", {"start": v(-46.17, -43.88) * mm, "end": v(-47.46, -45.02) * mm});
            skArc(sketch, "E54.18.2", {"start": v(-46.17, -43.88) * mm, "mid": v(-45.63, -42.83) * mm, "end": v(-45.17, -41.75) * mm});
            skArc(sketch, "E54.18.3", {"start": v(-45.17, -41.75) * mm, "mid": v(-45.13, -41.34) * mm, "end": v(-45.3, -40.97) * mm});
            skLineSegment(sketch, "E54.18.4", {"start": v(-45.3, -40.97) * mm, "end": v(-45.54, -40.67) * mm});
            skLineSegment(sketch, "E54.18.5", {"start": v(-45.8, -40.4) * mm, "end": v(-45.54, -40.67) * mm});
            skArc(sketch, "E54.18.6", {"start": v(-45.8, -40.4) * mm, "mid": v(-46.15, -40.17) * mm, "end": v(-46.56, -40.16) * mm});
            skLineSegment(sketch, "E54.18.7", {"start": v(-48.8, -40.89) * mm, "end": v(-50.1, -42.03) * mm});
            skArc(sketch, "E54.18.8", {"start": v(-48.8, -40.89) * mm, "mid": v(-47.7, -40.48) * mm, "end": v(-46.56, -40.16) * mm});
            skArc(sketch, "E54.18.9", {"start": v(-51.23, -41.93) * mm, "mid": v(-50.68, -42.22) * mm, "end": v(-50.1, -42.03) * mm});
            skArc(sketch, "E54.19.0", {"start": v(-41.5, -50.63) * mm, "mid": v(-41.69, -51.22) * mm, "end": v(-41.4, -51.76) * mm});
            skLineSegment(sketch, "E54.19.1", {"start": v(-40.35, -49.34) * mm, "end": v(-41.5, -50.63) * mm});
            skArc(sketch, "E54.19.2", {"start": v(-40.35, -49.34) * mm, "mid": v(-39.95, -48.23) * mm, "end": v(-39.63, -47.1) * mm});
            skArc(sketch, "E54.19.3", {"start": v(-39.63, -47.1) * mm, "mid": v(-39.64, -46.69) * mm, "end": v(-39.86, -46.34) * mm});
            skLineSegment(sketch, "E54.19.4", {"start": v(-39.86, -46.34) * mm, "end": v(-40.14, -46.08) * mm});
            skLineSegment(sketch, "E54.19.5", {"start": v(-40.43, -45.83) * mm, "end": v(-40.14, -46.08) * mm});
            skArc(sketch, "E54.19.6", {"start": v(-40.43, -45.83) * mm, "mid": v(-40.8, -45.66) * mm, "end": v(-41.21, -45.7) * mm});
            skLineSegment(sketch, "E54.19.7", {"start": v(-43.35, -46.7) * mm, "end": v(-44.49, -48) * mm});
            skArc(sketch, "E54.19.8", {"start": v(-43.35, -46.7) * mm, "mid": v(-42.3, -46.16) * mm, "end": v(-41.21, -45.7) * mm});
            skArc(sketch, "E54.19.9", {"start": v(-45.62, -48.04) * mm, "mid": v(-45.04, -48.26) * mm, "end": v(-44.49, -48) * mm});
            skArc(sketch, "E54.20.0", {"start": v(-34.87, -55.45) * mm, "mid": v(-34.99, -56.06) * mm, "end": v(-34.63, -56.56) * mm});
            skLineSegment(sketch, "E54.20.1", {"start": v(-33.9, -54.03) * mm, "end": v(-34.87, -55.45) * mm});
            skArc(sketch, "E54.20.2", {"start": v(-33.9, -54.03) * mm, "mid": v(-33.64, -52.88) * mm, "end": v(-33.46, -51.71) * mm});
            skArc(sketch, "E54.20.3", {"start": v(-33.46, -51.71) * mm, "mid": v(-33.53, -51.3) * mm, "end": v(-33.78, -50.99) * mm});
            skLineSegment(sketch, "E54.20.4", {"start": v(-33.78, -50.99) * mm, "end": v(-34.1, -50.76) * mm});
            skLineSegment(sketch, "E54.20.5", {"start": v(-34.42, -50.56) * mm, "end": v(-34.1, -50.76) * mm});
            skArc(sketch, "E54.20.6", {"start": v(-34.42, -50.56) * mm, "mid": v(-34.81, -50.43) * mm, "end": v(-35.21, -50.53) * mm});
            skLineSegment(sketch, "E54.20.7", {"start": v(-37.2, -51.79) * mm, "end": v(-38.17, -53.2) * mm});
            skArc(sketch, "E54.20.8", {"start": v(-37.2, -51.79) * mm, "mid": v(-36.23, -51.12) * mm, "end": v(-35.21, -50.53) * mm});
            skArc(sketch, "E54.20.9", {"start": v(-39.3, -53.4) * mm, "mid": v(-38.7, -53.54) * mm, "end": v(-38.17, -53.2) * mm});
            skArc(sketch, "E54.21.0", {"start": v(-27.7, -59.4) * mm, "mid": v(-27.74, -60.02) * mm, "end": v(-27.32, -60.48) * mm});
            skLineSegment(sketch, "E54.21.1", {"start": v(-26.91, -57.87) * mm, "end": v(-27.7, -59.4) * mm});
            skArc(sketch, "E54.21.2", {"start": v(-26.91, -57.87) * mm, "mid": v(-26.8, -56.7) * mm, "end": v(-26.77, -55.52) * mm});
            skArc(sketch, "E54.21.3", {"start": v(-26.77, -55.52) * mm, "mid": v(-26.88, -55.12) * mm, "end": v(-27.18, -54.84) * mm});
            skLineSegment(sketch, "E54.21.4", {"start": v(-27.18, -54.84) * mm, "end": v(-27.51, -54.65) * mm});
            skLineSegment(sketch, "E54.21.5", {"start": v(-27.86, -54.5) * mm, "end": v(-27.51, -54.65) * mm});
            skArc(sketch, "E54.21.6", {"start": v(-27.86, -54.5) * mm, "mid": v(-28.27, -54.42) * mm, "end": v(-28.65, -54.56) * mm});
            skLineSegment(sketch, "E54.21.7", {"start": v(-30.47, -56.06) * mm, "end": v(-31.25, -57.6) * mm});
            skArc(sketch, "E54.21.8", {"start": v(-30.47, -56.06) * mm, "mid": v(-29.59, -55.28) * mm, "end": v(-28.65, -54.56) * mm});
            skArc(sketch, "E54.21.9", {"start": v(-32.34, -57.92) * mm, "mid": v(-31.72, -57.99) * mm, "end": v(-31.25, -57.6) * mm});
            skArc(sketch, "E54.22.0", {"start": v(-20.08, -62.43) * mm, "mid": v(-20.05, -63.04) * mm, "end": v(-19.58, -63.44) * mm});
            skLineSegment(sketch, "E54.22.1", {"start": v(-19.5, -60.8) * mm, "end": v(-20.08, -62.43) * mm});
            skArc(sketch, "E54.22.2", {"start": v(-19.5, -60.8) * mm, "mid": v(-19.53, -59.63) * mm, "end": v(-19.65, -58.45) * mm});
            skArc(sketch, "E54.22.3", {"start": v(-19.65, -58.45) * mm, "mid": v(-19.81, -58.08) * mm, "end": v(-20.14, -57.83) * mm});
            skLineSegment(sketch, "E54.22.4", {"start": v(-20.14, -57.83) * mm, "end": v(-20.5, -57.7) * mm});
            skLineSegment(sketch, "E54.22.5", {"start": v(-20.86, -57.57) * mm, "end": v(-20.5, -57.7) * mm});
            skArc(sketch, "E54.22.6", {"start": v(-20.86, -57.57) * mm, "mid": v(-21.27, -57.55) * mm, "end": v(-21.64, -57.74) * mm});
            skLineSegment(sketch, "E54.22.7", {"start": v(-23.25, -59.45) * mm, "end": v(-23.84, -61.07) * mm});
            skArc(sketch, "E54.22.8", {"start": v(-23.25, -59.45) * mm, "mid": v(-22.48, -58.57) * mm, "end": v(-21.64, -57.74) * mm});
            skArc(sketch, "E54.22.9", {"start": v(-24.88, -61.54) * mm, "mid": v(-24.26, -61.53) * mm, "end": v(-23.84, -61.07) * mm});
            skArc(sketch, "E54.23.0", {"start": v(-12.15, -64.47) * mm, "mid": v(-12.04, -65.08) * mm, "end": v(-11.52, -65.42) * mm});
            skLineSegment(sketch, "E54.23.1", {"start": v(-11.78, -62.79) * mm, "end": v(-12.15, -64.47) * mm});
            skArc(sketch, "E54.23.2", {"start": v(-11.78, -62.79) * mm, "mid": v(-11.95, -61.62) * mm, "end": v(-12.22, -60.48) * mm});
            skArc(sketch, "E54.23.3", {"start": v(-12.22, -60.48) * mm, "mid": v(-12.43, -60.12) * mm, "end": v(-12.78, -59.92) * mm});
            skLineSegment(sketch, "E54.23.4", {"start": v(-12.78, -59.92) * mm, "end": v(-13.16, -59.82) * mm});
            skLineSegment(sketch, "E54.23.5", {"start": v(-13.53, -59.75) * mm, "end": v(-13.16, -59.82) * mm});
            skArc(sketch, "E54.23.6", {"start": v(-13.53, -59.75) * mm, "mid": v(-13.94, -59.78) * mm, "end": v(-14.28, -60.02) * mm});
            skLineSegment(sketch, "E54.23.7", {"start": v(-15.67, -61.92) * mm, "end": v(-16.04, -63.6) * mm});
            skArc(sketch, "E54.23.8", {"start": v(-15.67, -61.92) * mm, "mid": v(-15.01, -60.94) * mm, "end": v(-14.28, -60.02) * mm});
            skArc(sketch, "E54.23.9", {"start": v(-17.02, -64.19) * mm, "mid": v(-16.4, -64.1) * mm, "end": v(-16.04, -63.6) * mm});
            skArc(sketch, "E54.24.0", {"start": v(-4.03, -65.5) * mm, "mid": v(-3.84, -66.1) * mm, "end": v(-3.28, -66.36) * mm});
            skLineSegment(sketch, "E54.24.1", {"start": v(-3.86, -63.79) * mm, "end": v(-4.03, -65.5) * mm});
            skArc(sketch, "E54.24.2", {"start": v(-3.86, -63.79) * mm, "mid": v(-4.19, -62.65) * mm, "end": v(-4.6, -61.55) * mm});
            skArc(sketch, "E54.24.3", {"start": v(-4.6, -61.55) * mm, "mid": v(-4.84, -61.22) * mm, "end": v(-5.22, -61.07) * mm});
            skLineSegment(sketch, "E54.24.4", {"start": v(-5.22, -61.07) * mm, "end": v(-5.6, -61.02) * mm});
            skLineSegment(sketch, "E54.24.5", {"start": v(-5.99, -61) * mm, "end": v(-5.6, -61.02) * mm});
            skArc(sketch, "E54.24.6", {"start": v(-5.99, -61) * mm, "mid": v(-6.4, -61.08) * mm, "end": v(-6.7, -61.35) * mm});
            skLineSegment(sketch, "E54.24.7", {"start": v(-7.84, -63.41) * mm, "end": v(-8, -65.13) * mm});
            skArc(sketch, "E54.24.8", {"start": v(-7.84, -63.41) * mm, "mid": v(-7.3, -62.36) * mm, "end": v(-6.7, -61.35) * mm});
            skArc(sketch, "E54.24.9", {"start": v(-8.89, -65.83) * mm, "mid": v(-8.3, -65.67) * mm, "end": v(-8, -65.13) * mm});
            skArc(sketch, "E54.25.0", {"start": v(4.17, -65.5) * mm, "mid": v(4.43, -66.07) * mm, "end": v(5.01, -66.27) * mm});
            skLineSegment(sketch, "E54.25.1", {"start": v(4.11, -63.79) * mm, "end": v(4.17, -65.5) * mm});
            skArc(sketch, "E54.25.2", {"start": v(4.11, -63.79) * mm, "mid": v(3.65, -62.7) * mm, "end": v(3.1, -61.66) * mm});
            skArc(sketch, "E54.25.3", {"start": v(3.1, -61.66) * mm, "mid": v(2.82, -61.37) * mm, "end": v(2.42, -61.26) * mm});
            skLineSegment(sketch, "E54.25.4", {"start": v(2.42, -61.26) * mm, "end": v(2.04, -61.26) * mm});
            skLineSegment(sketch, "E54.25.5", {"start": v(1.65, -61.28) * mm, "end": v(2.04, -61.26) * mm});
            skArc(sketch, "E54.25.6", {"start": v(1.65, -61.28) * mm, "mid": v(1.26, -61.42) * mm, "end": v(1, -61.72) * mm});
            skLineSegment(sketch, "E54.25.7", {"start": v(0.12, -63.91) * mm, "end": v(0.18, -65.63) * mm});
            skArc(sketch, "E54.25.8", {"start": v(0.12, -63.91) * mm, "mid": v(0.52, -62.8) * mm, "end": v(1, -61.72) * mm});
            skArc(sketch, "E54.25.9", {"start": v(-0.62, -66.45) * mm, "mid": v(-0.05, -66.21) * mm, "end": v(0.18, -65.63) * mm});
            skArc(sketch, "E54.26.0", {"start": v(12.3, -64.49) * mm, "mid": v(12.62, -65.01) * mm, "end": v(13.23, -65.14) * mm});
            skLineSegment(sketch, "E54.26.1", {"start": v(12.02, -62.79) * mm, "end": v(12.3, -64.49) * mm});
            skArc(sketch, "E54.26.2", {"start": v(12.02, -62.79) * mm, "mid": v(11.43, -61.77) * mm, "end": v(10.76, -60.8) * mm});
            skArc(sketch, "E54.26.3", {"start": v(10.76, -60.8) * mm, "mid": v(10.44, -60.55) * mm, "end": v(10.03, -60.5) * mm});
            skLineSegment(sketch, "E54.26.4", {"start": v(10.03, -60.5) * mm, "end": v(9.65, -60.54) * mm});
            skLineSegment(sketch, "E54.26.5", {"start": v(9.27, -60.61) * mm, "end": v(9.65, -60.54) * mm});
            skArc(sketch, "E54.26.6", {"start": v(9.27, -60.61) * mm, "mid": v(8.9, -60.8) * mm, "end": v(8.67, -61.13) * mm});
            skLineSegment(sketch, "E54.26.7", {"start": v(8.08, -63.41) * mm, "end": v(8.35, -65.11) * mm});
            skArc(sketch, "E54.26.8", {"start": v(8.08, -63.41) * mm, "mid": v(8.34, -62.26) * mm, "end": v(8.67, -61.13) * mm});
            skArc(sketch, "E54.26.9", {"start": v(7.66, -66.02) * mm, "mid": v(8.2, -65.71) * mm, "end": v(8.35, -65.11) * mm});
            skArc(sketch, "E54.27.0", {"start": v(20.23, -62.46) * mm, "mid": v(20.62, -62.94) * mm, "end": v(21.24, -62.99) * mm});
            skLineSegment(sketch, "E54.27.1", {"start": v(19.75, -60.8) * mm, "end": v(20.23, -62.46) * mm});
            skArc(sketch, "E54.27.2", {"start": v(19.75, -60.8) * mm, "mid": v(19.03, -59.87) * mm, "end": v(18.24, -59) * mm});
            skArc(sketch, "E54.27.3", {"start": v(18.24, -59) * mm, "mid": v(17.9, -58.78) * mm, "end": v(17.48, -58.78) * mm});
            skLineSegment(sketch, "E54.27.4", {"start": v(17.48, -58.78) * mm, "end": v(17.1, -58.87) * mm});
            skLineSegment(sketch, "E54.27.5", {"start": v(16.74, -59) * mm, "end": v(17.1, -58.87) * mm});
            skArc(sketch, "E54.27.6", {"start": v(16.74, -59) * mm, "mid": v(16.4, -59.22) * mm, "end": v(16.22, -59.58) * mm});
            skLineSegment(sketch, "E54.27.7", {"start": v(15.92, -61.92) * mm, "end": v(16.4, -63.57) * mm});
            skArc(sketch, "E54.27.8", {"start": v(15.92, -61.92) * mm, "mid": v(16.02, -60.74) * mm, "end": v(16.22, -59.58) * mm});
            skArc(sketch, "E54.27.9", {"start": v(15.83, -64.56) * mm, "mid": v(16.32, -64.19) * mm, "end": v(16.4, -63.57) * mm});
            skArc(sketch, "E54.28.0", {"start": v(27.85, -59.45) * mm, "mid": v(28.3, -59.88) * mm, "end": v(28.91, -59.85) * mm});
            skLineSegment(sketch, "E54.28.1", {"start": v(27.16, -57.87) * mm, "end": v(27.85, -59.45) * mm});
            skArc(sketch, "E54.28.2", {"start": v(27.16, -57.87) * mm, "mid": v(26.33, -57.03) * mm, "end": v(25.44, -56.26) * mm});
            skArc(sketch, "E54.28.3", {"start": v(25.44, -56.26) * mm, "mid": v(25.07, -56.1) * mm, "end": v(24.66, -56.14) * mm});
            skLineSegment(sketch, "E54.28.4", {"start": v(24.66, -56.14) * mm, "end": v(24.3, -56.28) * mm});
            skLineSegment(sketch, "E54.28.5", {"start": v(23.95, -56.45) * mm, "end": v(24.3, -56.28) * mm});
            skArc(sketch, "E54.28.6", {"start": v(23.95, -56.45) * mm, "mid": v(23.64, -56.71) * mm, "end": v(23.5, -57.1) * mm});
            skLineSegment(sketch, "E54.28.7", {"start": v(23.5, -59.45) * mm, "end": v(24.18, -61.03) * mm});
            skArc(sketch, "E54.28.8", {"start": v(23.5, -59.45) * mm, "mid": v(23.46, -58.28) * mm, "end": v(23.5, -57.1) * mm});
            skArc(sketch, "E54.28.9", {"start": v(23.74, -62.08) * mm, "mid": v(24.19, -61.65) * mm, "end": v(24.18, -61.03) * mm});
            skArc(sketch, "E54.29.0", {"start": v(35.03, -55.5) * mm, "mid": v(35.52, -55.88) * mm, "end": v(36.13, -55.77) * mm});
            skLineSegment(sketch, "E54.29.1", {"start": v(34.15, -54.03) * mm, "end": v(35.03, -55.5) * mm});
            skArc(sketch, "E54.29.2", {"start": v(34.15, -54.03) * mm, "mid": v(33.22, -53.3) * mm, "end": v(32.24, -52.65) * mm});
            skArc(sketch, "E54.29.3", {"start": v(32.24, -52.65) * mm, "mid": v(31.85, -52.53) * mm, "end": v(31.45, -52.63) * mm});
            skLineSegment(sketch, "E54.29.4", {"start": v(31.45, -52.63) * mm, "end": v(31.11, -52.81) * mm});
            skLineSegment(sketch, "E54.29.5", {"start": v(30.79, -53.02) * mm, "end": v(31.11, -52.81) * mm});
            skArc(sketch, "E54.29.6", {"start": v(30.79, -53.02) * mm, "mid": v(30.51, -53.32) * mm, "end": v(30.42, -53.72) * mm});
            skLineSegment(sketch, "E54.29.7", {"start": v(30.72, -56.06) * mm, "end": v(31.6, -57.54) * mm});
            skArc(sketch, "E54.29.8", {"start": v(30.72, -56.06) * mm, "mid": v(30.53, -54.9) * mm, "end": v(30.42, -53.72) * mm});
            skArc(sketch, "E54.29.9", {"start": v(31.29, -58.64) * mm, "mid": v(31.67, -58.15) * mm, "end": v(31.6, -57.54) * mm});
            skArc(sketch, "E54.30.0", {"start": v(41.66, -50.7) * mm, "mid": v(42.2, -51) * mm, "end": v(42.79, -50.82) * mm});
            skLineSegment(sketch, "E54.30.1", {"start": v(40.6, -49.34) * mm, "end": v(41.66, -50.7) * mm});
            skArc(sketch, "E54.30.2", {"start": v(40.6, -49.34) * mm, "mid": v(39.59, -48.74) * mm, "end": v(38.54, -48.2) * mm});
            skArc(sketch, "E54.30.3", {"start": v(38.54, -48.2) * mm, "mid": v(38.13, -48.14) * mm, "end": v(37.75, -48.29) * mm});
            skLineSegment(sketch, "E54.30.4", {"start": v(37.75, -48.29) * mm, "end": v(37.44, -48.51) * mm});
            skLineSegment(sketch, "E54.30.5", {"start": v(37.14, -48.76) * mm, "end": v(37.44, -48.51) * mm});
            skArc(sketch, "E54.30.6", {"start": v(37.14, -48.76) * mm, "mid": v(36.9, -49.1) * mm, "end": v(36.87, -49.5) * mm});
            skLineSegment(sketch, "E54.30.7", {"start": v(37.45, -51.79) * mm, "end": v(38.5, -53.15) * mm});
            skArc(sketch, "E54.30.8", {"start": v(37.45, -51.79) * mm, "mid": v(37.12, -50.65) * mm, "end": v(36.87, -49.5) * mm});
            skArc(sketch, "E54.30.9", {"start": v(38.34, -54.27) * mm, "mid": v(38.66, -53.74) * mm, "end": v(38.5, -53.15) * mm});
            skArc(sketch, "E54.31.0", {"start": v(47.63, -45.1) * mm, "mid": v(48.2, -45.33) * mm, "end": v(48.77, -45.07) * mm});
            skLineSegment(sketch, "E54.31.1", {"start": v(46.41, -43.88) * mm, "end": v(47.63, -45.1) * mm});
            skArc(sketch, "E54.31.2", {"start": v(46.41, -43.88) * mm, "mid": v(45.34, -43.4) * mm, "end": v(44.22, -43.02) * mm});
            skArc(sketch, "E54.31.3", {"start": v(44.22, -43.02) * mm, "mid": v(43.81, -43) * mm, "end": v(43.45, -43.2) * mm});
            skLineSegment(sketch, "E54.31.4", {"start": v(43.45, -43.2) * mm, "end": v(43.17, -43.46) * mm});
            skLineSegment(sketch, "E54.31.5", {"start": v(42.9, -43.74) * mm, "end": v(43.17, -43.46) * mm});
            skArc(sketch, "E54.31.6", {"start": v(42.9, -43.74) * mm, "mid": v(42.72, -44.1) * mm, "end": v(42.73, -44.51) * mm});
            skLineSegment(sketch, "E54.31.7", {"start": v(43.6, -46.7) * mm, "end": v(44.81, -47.92) * mm});
            skArc(sketch, "E54.31.8", {"start": v(43.6, -46.7) * mm, "mid": v(43.12, -45.62) * mm, "end": v(42.73, -44.51) * mm});
            skArc(sketch, "E54.31.9", {"start": v(44.79, -49.06) * mm, "mid": v(45.04, -48.5) * mm, "end": v(44.81, -47.92) * mm});
            skArc(sketch, "E54.32.0", {"start": v(52.86, -38.8) * mm, "mid": v(53.46, -38.95) * mm, "end": v(53.98, -38.63) * mm});
            skLineSegment(sketch, "E54.32.1", {"start": v(51.5, -37.74) * mm, "end": v(52.86, -38.8) * mm});
            skArc(sketch, "E54.32.2", {"start": v(51.5, -37.74) * mm, "mid": v(50.37, -37.4) * mm, "end": v(49.22, -37.15) * mm});
            skArc(sketch, "E54.32.3", {"start": v(49.22, -37.15) * mm, "mid": v(48.8, -37.2) * mm, "end": v(48.47, -37.43) * mm});
            skLineSegment(sketch, "E54.32.4", {"start": v(48.47, -37.43) * mm, "end": v(48.23, -37.72) * mm});
            skLineSegment(sketch, "E54.32.5", {"start": v(48, -38.03) * mm, "end": v(48.23, -37.72) * mm});
            skArc(sketch, "E54.32.6", {"start": v(48, -38.03) * mm, "mid": v(47.86, -38.42) * mm, "end": v(47.92, -38.82) * mm});
            skLineSegment(sketch, "E54.32.7", {"start": v(49.05, -40.89) * mm, "end": v(50.41, -41.94) * mm});
            skArc(sketch, "E54.32.8", {"start": v(49.05, -40.89) * mm, "mid": v(48.45, -39.88) * mm, "end": v(47.92, -38.82) * mm});
            skArc(sketch, "E54.32.9", {"start": v(50.53, -43.07) * mm, "mid": v(50.71, -42.48) * mm, "end": v(50.41, -41.94) * mm});
            skArc(sketch, "E54.33.0", {"start": v(57.25, -31.88) * mm, "mid": v(57.87, -31.96) * mm, "end": v(58.35, -31.57) * mm});
            skLineSegment(sketch, "E54.33.1", {"start": v(55.77, -31) * mm, "end": v(57.25, -31.88) * mm});
            skArc(sketch, "E54.33.2", {"start": v(55.77, -31) * mm, "mid": v(54.6, -30.81) * mm, "end": v(53.43, -30.71) * mm});
            skArc(sketch, "E54.33.3", {"start": v(53.43, -30.71) * mm, "mid": v(53.03, -30.8) * mm, "end": v(52.73, -31.08) * mm});
            skLineSegment(sketch, "E54.33.4", {"start": v(52.73, -31.08) * mm, "end": v(52.52, -31.4) * mm});
            skLineSegment(sketch, "E54.33.5", {"start": v(52.34, -31.74) * mm, "end": v(52.52, -31.4) * mm});
            skArc(sketch, "E54.33.6", {"start": v(52.34, -31.74) * mm, "mid": v(52.24, -32.14) * mm, "end": v(52.36, -32.53) * mm});
            skLineSegment(sketch, "E54.33.7", {"start": v(53.74, -34.44) * mm, "end": v(55.22, -35.31) * mm});
            skArc(sketch, "E54.33.8", {"start": v(53.74, -34.44) * mm, "mid": v(53.01, -33.5) * mm, "end": v(52.36, -32.53) * mm});
            skArc(sketch, "E54.33.9", {"start": v(55.48, -36.42) * mm, "mid": v(55.59, -35.81) * mm, "end": v(55.22, -35.31) * mm});
            skArc(sketch, "E54.34.0", {"start": v(60.75, -24.47) * mm, "mid": v(61.37, -24.47) * mm, "end": v(61.8, -24.03) * mm});
            skLineSegment(sketch, "E54.34.1", {"start": v(59.17, -23.79) * mm, "end": v(60.75, -24.47) * mm});
            skArc(sketch, "E54.34.2", {"start": v(59.17, -23.79) * mm, "mid": v(57.99, -23.75) * mm, "end": v(56.81, -23.8) * mm});
            skArc(sketch, "E54.34.3", {"start": v(56.81, -23.8) * mm, "mid": v(56.42, -23.93) * mm, "end": v(56.16, -24.24) * mm});
            skLineSegment(sketch, "E54.34.4", {"start": v(56.16, -24.24) * mm, "end": v(56, -24.59) * mm});
            skLineSegment(sketch, "E54.34.5", {"start": v(55.85, -24.95) * mm, "end": v(56, -24.59) * mm});
            skArc(sketch, "E54.34.6", {"start": v(55.85, -24.95) * mm, "mid": v(55.8, -25.35) * mm, "end": v(55.97, -25.73) * mm});
            skLineSegment(sketch, "E54.34.7", {"start": v(57.58, -27.45) * mm, "end": v(59.16, -28.13) * mm});
            skArc(sketch, "E54.34.8", {"start": v(57.58, -27.45) * mm, "mid": v(56.75, -26.62) * mm, "end": v(55.97, -25.73) * mm});
            skArc(sketch, "E54.34.9", {"start": v(59.56, -29.2) * mm, "mid": v(59.59, -28.58) * mm, "end": v(59.16, -28.13) * mm});
            skArc(sketch, "E54.35.0", {"start": v(63.28, -16.68) * mm, "mid": v(63.9, -16.6) * mm, "end": v(64.27, -16.11) * mm});
            skLineSegment(sketch, "E54.35.1", {"start": v(61.63, -16.2) * mm, "end": v(63.28, -16.68) * mm});
            skArc(sketch, "E54.35.2", {"start": v(61.63, -16.2) * mm, "mid": v(60.46, -16.3) * mm, "end": v(59.3, -16.5) * mm});
            skArc(sketch, "E54.35.3", {"start": v(59.3, -16.5) * mm, "mid": v(58.93, -16.69) * mm, "end": v(58.7, -17.03) * mm});
            skLineSegment(sketch, "E54.35.4", {"start": v(58.7, -17.03) * mm, "end": v(58.59, -17.4) * mm});
            skLineSegment(sketch, "E54.35.5", {"start": v(58.49, -17.77) * mm, "end": v(58.59, -17.4) * mm});
            skArc(sketch, "E54.35.6", {"start": v(58.49, -17.77) * mm, "mid": v(58.5, -18.18) * mm, "end": v(58.7, -18.53) * mm});
            skLineSegment(sketch, "E54.35.7", {"start": v(60.52, -20.03) * mm, "end": v(62.17, -20.51) * mm});
            skArc(sketch, "E54.35.8", {"start": v(60.52, -20.03) * mm, "mid": v(59.58, -19.32) * mm, "end": v(58.7, -18.53) * mm});
            skArc(sketch, "E54.35.9", {"start": v(62.7, -21.52) * mm, "mid": v(62.65, -20.9) * mm, "end": v(62.17, -20.51) * mm});
            skArc(sketch, "E54.36.0", {"start": v(64.83, -8.64) * mm, "mid": v(65.43, -8.49) * mm, "end": v(65.73, -7.95) * mm});
            skLineSegment(sketch, "E54.36.1", {"start": v(63.13, -8.37) * mm, "end": v(64.83, -8.64) * mm});
            skArc(sketch, "E54.36.2", {"start": v(63.13, -8.37) * mm, "mid": v(61.97, -8.62) * mm, "end": v(60.85, -8.96) * mm});
            skArc(sketch, "E54.36.3", {"start": v(60.85, -8.96) * mm, "mid": v(60.5, -9.19) * mm, "end": v(60.33, -9.56) * mm});
            skLineSegment(sketch, "E54.36.4", {"start": v(60.33, -9.56) * mm, "end": v(60.25, -9.93) * mm});
            skLineSegment(sketch, "E54.36.5", {"start": v(60.2, -10.32) * mm, "end": v(60.25, -9.93) * mm});
            skArc(sketch, "E54.36.6", {"start": v(60.2, -10.32) * mm, "mid": v(60.26, -10.72) * mm, "end": v(60.52, -11.04) * mm});
            skLineSegment(sketch, "E54.36.7", {"start": v(62.5, -12.3) * mm, "end": v(64.2, -12.58) * mm});
            skArc(sketch, "E54.36.8", {"start": v(62.5, -12.3) * mm, "mid": v(61.48, -11.71) * mm, "end": v(60.52, -11.04) * mm});
            skArc(sketch, "E54.36.9", {"start": v(64.85, -13.51) * mm, "mid": v(64.73, -12.9) * mm, "end": v(64.2, -12.58) * mm});
            skArc(sketch, "E54.37.0", {"start": v(65.35, -0.46) * mm, "mid": v(65.92, -0.24) * mm, "end": v(66.16, 0.33) * mm});
            skLineSegment(sketch, "E54.37.1", {"start": v(63.63, -0.41) * mm, "end": v(65.35, -0.46) * mm});
            skArc(sketch, "E54.37.2", {"start": v(63.63, -0.41) * mm, "mid": v(62.52, -0.8) * mm, "end": v(61.44, -1.28) * mm});
            skArc(sketch, "E54.37.3", {"start": v(61.44, -1.28) * mm, "mid": v(61.13, -1.55) * mm, "end": v(61, -1.94) * mm});
            skLineSegment(sketch, "E54.37.4", {"start": v(61, -1.94) * mm, "end": v(60.97, -2.32) * mm});
            skLineSegment(sketch, "E54.37.5", {"start": v(60.97, -2.7) * mm, "end": v(60.97, -2.32) * mm});
            skArc(sketch, "E54.37.6", {"start": v(60.97, -2.7) * mm, "mid": v(61.08, -3.1) * mm, "end": v(61.37, -3.4) * mm});
            skLineSegment(sketch, "E54.37.7", {"start": v(63.5, -4.4) * mm, "end": v(65.22, -4.45) * mm});
            skArc(sketch, "E54.37.8", {"start": v(63.5, -4.4) * mm, "mid": v(62.42, -3.93) * mm, "end": v(61.37, -3.4) * mm});
            skArc(sketch, "E54.37.9", {"start": v(65.98, -5.3) * mm, "mid": v(65.78, -4.71) * mm, "end": v(65.22, -4.45) * mm});
            skArc(sketch, "E54.38.0", {"start": v(64.84, 7.71) * mm, "mid": v(65.38, 8) * mm, "end": v(65.55, 8.6) * mm});
            skLineSegment(sketch, "E54.38.1", {"start": v(63.13, 7.55) * mm, "end": v(64.84, 7.71) * mm});
            skArc(sketch, "E54.38.2", {"start": v(63.13, 7.55) * mm, "mid": v(62.07, 7.02) * mm, "end": v(61.06, 6.41) * mm});
            skArc(sketch, "E54.38.3", {"start": v(61.06, 6.41) * mm, "mid": v(60.8, 6.1) * mm, "end": v(60.7, 5.7) * mm});
            skLineSegment(sketch, "E54.38.4", {"start": v(60.7, 5.7) * mm, "end": v(60.73, 5.32) * mm});
            skLineSegment(sketch, "E54.38.5", {"start": v(60.78, 4.94) * mm, "end": v(60.73, 5.32) * mm});
            skArc(sketch, "E54.38.6", {"start": v(60.78, 4.94) * mm, "mid": v(60.94, 4.56) * mm, "end": v(61.26, 4.3) * mm});
            skLineSegment(sketch, "E54.38.7", {"start": v(63.5, 3.58) * mm, "end": v(65.22, 3.74) * mm});
            skArc(sketch, "E54.38.8", {"start": v(63.5, 3.58) * mm, "mid": v(62.37, 3.9) * mm, "end": v(61.26, 4.3) * mm});
            skArc(sketch, "E54.38.9", {"start": v(66.08, 3) * mm, "mid": v(65.8, 3.55) * mm, "end": v(65.22, 3.74) * mm});
            skArc(sketch, "E54.39.0", {"start": v(63.31, 15.76) * mm, "mid": v(63.81, 16.12) * mm, "end": v(63.9, 16.73) * mm});
            skLineSegment(sketch, "E54.39.1", {"start": v(61.63, 15.38) * mm, "end": v(63.31, 15.76) * mm});
            skArc(sketch, "E54.39.2", {"start": v(61.63, 15.38) * mm, "mid": v(60.65, 14.72) * mm, "end": v(59.73, 14) * mm});
            skArc(sketch, "E54.39.3", {"start": v(59.73, 14) * mm, "mid": v(59.5, 13.66) * mm, "end": v(59.46, 13.25) * mm});
            skLineSegment(sketch, "E54.39.4", {"start": v(59.46, 13.25) * mm, "end": v(59.54, 12.87) * mm});
            skLineSegment(sketch, "E54.39.5", {"start": v(59.63, 12.5) * mm, "end": v(59.54, 12.87) * mm});
            skArc(sketch, "E54.39.6", {"start": v(59.63, 12.5) * mm, "mid": v(59.83, 12.14) * mm, "end": v(60.19, 11.93) * mm});
            skLineSegment(sketch, "E54.39.7", {"start": v(62.5, 11.49) * mm, "end": v(64.18, 11.86) * mm});
            skArc(sketch, "E54.39.8", {"start": v(62.5, 11.49) * mm, "mid": v(61.34, 11.67) * mm, "end": v(60.19, 11.93) * mm});
            skArc(sketch, "E54.39.9", {"start": v(65.13, 11.23) * mm, "mid": v(64.79, 11.75) * mm, "end": v(64.18, 11.86) * mm});
            skArc(sketch, "E54.40.0", {"start": v(60.79, 23.55) * mm, "mid": v(61.24, 23.97) * mm, "end": v(61.25, 24.59) * mm});
            skLineSegment(sketch, "E54.40.1", {"start": v(59.17, 22.97) * mm, "end": v(60.79, 23.55) * mm});
            skArc(sketch, "E54.40.2", {"start": v(59.17, 22.97) * mm, "mid": v(58.28, 22.2) * mm, "end": v(57.45, 21.35) * mm});
            skArc(sketch, "E54.40.3", {"start": v(57.45, 21.35) * mm, "mid": v(57.26, 20.99) * mm, "end": v(57.28, 20.58) * mm});
            skLineSegment(sketch, "E54.40.4", {"start": v(57.28, 20.58) * mm, "end": v(57.4, 20.21) * mm});
            skLineSegment(sketch, "E54.40.5", {"start": v(57.54, 19.85) * mm, "end": v(57.4, 20.21) * mm});
            skArc(sketch, "E54.40.6", {"start": v(57.54, 19.85) * mm, "mid": v(57.8, 19.53) * mm, "end": v(58.17, 19.36) * mm});
            skLineSegment(sketch, "E54.40.7", {"start": v(60.52, 19.21) * mm, "end": v(62.14, 19.8) * mm});
            skArc(sketch, "E54.40.8", {"start": v(60.52, 19.21) * mm, "mid": v(59.34, 19.24) * mm, "end": v(58.17, 19.36) * mm});
            skArc(sketch, "E54.40.9", {"start": v(63.16, 19.3) * mm, "mid": v(62.76, 19.76) * mm, "end": v(62.14, 19.8) * mm});
            skArc(sketch, "E54.41.0", {"start": v(57.3, 30.96) * mm, "mid": v(57.7, 31.44) * mm, "end": v(57.63, 32.05) * mm});
            skLineSegment(sketch, "E54.41.1", {"start": v(55.77, 30.18) * mm, "end": v(57.3, 30.96) * mm});
            skArc(sketch, "E54.41.2", {"start": v(55.77, 30.18) * mm, "mid": v(54.99, 29.3) * mm, "end": v(54.27, 28.37) * mm});
            skArc(sketch, "E54.41.3", {"start": v(54.27, 28.37) * mm, "mid": v(54.13, 27.98) * mm, "end": v(54.2, 27.58) * mm});
            skLineSegment(sketch, "E54.41.4", {"start": v(54.2, 27.58) * mm, "end": v(54.37, 27.23) * mm});
            skLineSegment(sketch, "E54.41.5", {"start": v(54.55, 26.9) * mm, "end": v(54.37, 27.23) * mm});
            skArc(sketch, "E54.41.6", {"start": v(54.55, 26.9) * mm, "mid": v(54.84, 26.6) * mm, "end": v(55.23, 26.48) * mm});
            skLineSegment(sketch, "E54.41.7", {"start": v(57.58, 26.63) * mm, "end": v(59.12, 27.4) * mm});
            skArc(sketch, "E54.41.8", {"start": v(57.58, 26.63) * mm, "mid": v(56.4, 26.51) * mm, "end": v(55.23, 26.48) * mm});
            skArc(sketch, "E54.41.9", {"start": v(60.2, 27.03) * mm, "mid": v(59.73, 27.45) * mm, "end": v(59.12, 27.4) * mm});
            skArc(sketch, "E54.42.0", {"start": v(52.92, 37.88) * mm, "mid": v(53.26, 38.4) * mm, "end": v(53.11, 39) * mm});
            skLineSegment(sketch, "E54.42.1", {"start": v(51.5, 36.92) * mm, "end": v(52.92, 37.88) * mm});
            skArc(sketch, "E54.42.2", {"start": v(51.5, 36.92) * mm, "mid": v(50.83, 35.94) * mm, "end": v(50.24, 34.92) * mm});
            skArc(sketch, "E54.42.3", {"start": v(50.24, 34.92) * mm, "mid": v(50.15, 34.52) * mm, "end": v(50.27, 34.13) * mm});
            skLineSegment(sketch, "E54.42.4", {"start": v(50.27, 34.13) * mm, "end": v(50.48, 33.8) * mm});
            skLineSegment(sketch, "E54.42.5", {"start": v(50.7, 33.5) * mm, "end": v(50.48, 33.8) * mm});
            skArc(sketch, "E54.42.6", {"start": v(50.7, 33.5) * mm, "mid": v(51.02, 33.24) * mm, "end": v(51.43, 33.18) * mm});
            skLineSegment(sketch, "E54.42.7", {"start": v(53.74, 33.62) * mm, "end": v(55.16, 34.58) * mm});
            skArc(sketch, "E54.42.8", {"start": v(53.74, 33.62) * mm, "mid": v(52.6, 33.35) * mm, "end": v(51.43, 33.18) * mm});
            skArc(sketch, "E54.42.9", {"start": v(56.28, 34.35) * mm, "mid": v(55.77, 34.7) * mm, "end": v(55.16, 34.58) * mm});
            skArc(sketch, "E54.43.0", {"start": v(47.7, 44.2) * mm, "mid": v(47.97, 44.76) * mm, "end": v(47.75, 45.33) * mm});
            skLineSegment(sketch, "E54.43.1", {"start": v(46.42, 43.06) * mm, "end": v(47.7, 44.2) * mm});
            skArc(sketch, "E54.43.2", {"start": v(46.42, 43.06) * mm, "mid": v(45.88, 42.01) * mm, "end": v(45.42, 40.93) * mm});
            skArc(sketch, "E54.43.3", {"start": v(45.42, 40.93) * mm, "mid": v(45.37, 40.52) * mm, "end": v(45.54, 40.15) * mm});
            skLineSegment(sketch, "E54.43.4", {"start": v(45.54, 40.15) * mm, "end": v(45.79, 39.85) * mm});
            skLineSegment(sketch, "E54.43.5", {"start": v(46.05, 39.57) * mm, "end": v(45.79, 39.85) * mm});
            skArc(sketch, "E54.43.6", {"start": v(46.05, 39.57) * mm, "mid": v(46.4, 39.35) * mm, "end": v(46.81, 39.34) * mm});
            skLineSegment(sketch, "E54.43.7", {"start": v(49.05, 40.07) * mm, "end": v(50.35, 41.2) * mm});
            skArc(sketch, "E54.43.8", {"start": v(49.05, 40.07) * mm, "mid": v(47.95, 39.66) * mm, "end": v(46.81, 39.34) * mm});
            skArc(sketch, "E54.43.9", {"start": v(51.48, 41.11) * mm, "mid": v(50.93, 41.4) * mm, "end": v(50.35, 41.2) * mm});
            skArc(sketch, "E54.44.0", {"start": v(41.74, 49.81) * mm, "mid": v(41.93, 50.4) * mm, "end": v(41.65, 50.94) * mm});
            skLineSegment(sketch, "E54.44.1", {"start": v(40.6, 48.52) * mm, "end": v(41.74, 49.81) * mm});
            skArc(sketch, "E54.44.2", {"start": v(40.6, 48.52) * mm, "mid": v(40.2, 47.41) * mm, "end": v(39.88, 46.28) * mm});
            skArc(sketch, "E54.44.3", {"start": v(39.88, 46.28) * mm, "mid": v(39.89, 45.87) * mm, "end": v(40.1, 45.52) * mm});
            skLineSegment(sketch, "E54.44.4", {"start": v(40.1, 45.52) * mm, "end": v(40.38, 45.26) * mm});
            skLineSegment(sketch, "E54.44.5", {"start": v(40.68, 45.01) * mm, "end": v(40.38, 45.26) * mm});
            skArc(sketch, "E54.44.6", {"start": v(40.68, 45.01) * mm, "mid": v(41.05, 44.84) * mm, "end": v(41.46, 44.88) * mm});
            skLineSegment(sketch, "E54.44.7", {"start": v(43.6, 45.88) * mm, "end": v(44.73, 47.17) * mm});
            skArc(sketch, "E54.44.8", {"start": v(43.6, 45.88) * mm, "mid": v(42.55, 45.34) * mm, "end": v(41.46, 44.88) * mm});
            skArc(sketch, "E54.44.9", {"start": v(45.87, 47.22) * mm, "mid": v(45.3, 47.44) * mm, "end": v(44.73, 47.17) * mm});
            skArc(sketch, "E54.45.0", {"start": v(35.12, 54.63) * mm, "mid": v(35.24, 55.24) * mm, "end": v(34.88, 55.74) * mm});
            skLineSegment(sketch, "E54.45.1", {"start": v(34.15, 53.2) * mm, "end": v(35.12, 54.63) * mm});
            skArc(sketch, "E54.45.2", {"start": v(34.15, 53.2) * mm, "mid": v(33.89, 52.06) * mm, "end": v(33.71, 50.9) * mm});
            skArc(sketch, "E54.45.3", {"start": v(33.71, 50.9) * mm, "mid": v(33.77, 50.49) * mm, "end": v(34.03, 50.17) * mm});
            skLineSegment(sketch, "E54.45.4", {"start": v(34.03, 50.17) * mm, "end": v(34.34, 49.94) * mm});
            skLineSegment(sketch, "E54.45.5", {"start": v(34.67, 49.74) * mm, "end": v(34.34, 49.94) * mm});
            skArc(sketch, "E54.45.6", {"start": v(34.67, 49.74) * mm, "mid": v(35.06, 49.61) * mm, "end": v(35.46, 49.7) * mm});
            skLineSegment(sketch, "E54.45.7", {"start": v(37.45, 50.96) * mm, "end": v(38.42, 52.39) * mm});
            skArc(sketch, "E54.45.8", {"start": v(37.45, 50.96) * mm, "mid": v(36.48, 50.3) * mm, "end": v(35.46, 49.7) * mm});
            skArc(sketch, "E54.45.9", {"start": v(39.54, 52.58) * mm, "mid": v(38.94, 52.72) * mm, "end": v(38.42, 52.39) * mm});
            skArc(sketch, "E54.46.0", {"start": v(27.94, 58.58) * mm, "mid": v(27.99, 59.2) * mm, "end": v(27.57, 59.66) * mm});
            skLineSegment(sketch, "E54.46.1", {"start": v(27.16, 57.05) * mm, "end": v(27.94, 58.58) * mm});
            skArc(sketch, "E54.46.2", {"start": v(27.16, 57.05) * mm, "mid": v(27.05, 55.88) * mm, "end": v(27.02, 54.7) * mm});
            skArc(sketch, "E54.46.3", {"start": v(27.02, 54.7) * mm, "mid": v(27.13, 54.3) * mm, "end": v(27.43, 54.02) * mm});
            skLineSegment(sketch, "E54.46.4", {"start": v(27.43, 54.02) * mm, "end": v(27.76, 53.83) * mm});
            skLineSegment(sketch, "E54.46.5", {"start": v(28.1, 53.67) * mm, "end": v(27.76, 53.83) * mm});
            skArc(sketch, "E54.46.6", {"start": v(28.1, 53.67) * mm, "mid": v(28.51, 53.6) * mm, "end": v(28.9, 53.74) * mm});
            skLineSegment(sketch, "E54.46.7", {"start": v(30.72, 55.24) * mm, "end": v(31.5, 56.77) * mm});
            skArc(sketch, "E54.46.8", {"start": v(30.72, 55.24) * mm, "mid": v(29.84, 54.45) * mm, "end": v(28.9, 53.74) * mm});
            skArc(sketch, "E54.46.9", {"start": v(32.59, 57.1) * mm, "mid": v(31.97, 57.17) * mm, "end": v(31.5, 56.77) * mm});
            skArc(sketch, "E54.47.0", {"start": v(20.33, 61.6) * mm, "mid": v(20.3, 62.22) * mm, "end": v(19.82, 62.62) * mm});
            skLineSegment(sketch, "E54.47.1", {"start": v(19.75, 59.98) * mm, "end": v(20.33, 61.6) * mm});
            skArc(sketch, "E54.47.2", {"start": v(19.75, 59.98) * mm, "mid": v(19.78, 58.8) * mm, "end": v(19.9, 57.63) * mm});
            skArc(sketch, "E54.47.3", {"start": v(19.9, 57.63) * mm, "mid": v(20.06, 57.26) * mm, "end": v(20.39, 57.01) * mm});
            skLineSegment(sketch, "E54.47.4", {"start": v(20.39, 57.01) * mm, "end": v(20.75, 56.87) * mm});
            skLineSegment(sketch, "E54.47.5", {"start": v(21.11, 56.75) * mm, "end": v(20.75, 56.87) * mm});
            skArc(sketch, "E54.47.6", {"start": v(21.11, 56.75) * mm, "mid": v(21.52, 56.73) * mm, "end": v(21.89, 56.92) * mm});
            skLineSegment(sketch, "E54.47.7", {"start": v(23.5, 58.63) * mm, "end": v(24.08, 60.25) * mm});
            skArc(sketch, "E54.47.8", {"start": v(23.5, 58.63) * mm, "mid": v(22.72, 57.75) * mm, "end": v(21.89, 56.92) * mm});
            skArc(sketch, "E54.47.9", {"start": v(25.12, 60.71) * mm, "mid": v(24.5, 60.7) * mm, "end": v(24.08, 60.25) * mm});
            skArc(sketch, "E54.48.0", {"start": v(12.4, 63.65) * mm, "mid": v(12.29, 64.26) * mm, "end": v(11.77, 64.6) * mm});
            skLineSegment(sketch, "E54.48.1", {"start": v(12.02, 61.97) * mm, "end": v(12.4, 63.65) * mm});
            skArc(sketch, "E54.48.2", {"start": v(12.02, 61.97) * mm, "mid": v(12.2, 60.8) * mm, "end": v(12.47, 59.65) * mm});
            skArc(sketch, "E54.48.3", {"start": v(12.47, 59.65) * mm, "mid": v(12.67, 59.3) * mm, "end": v(13.03, 59.1) * mm});
            skLineSegment(sketch, "E54.48.4", {"start": v(13.03, 59.1) * mm, "end": v(13.4, 59) * mm});
            skLineSegment(sketch, "E54.48.5", {"start": v(13.78, 58.93) * mm, "end": v(13.4, 59) * mm});
            skArc(sketch, "E54.48.6", {"start": v(13.78, 58.93) * mm, "mid": v(14.2, 58.96) * mm, "end": v(14.53, 59.2) * mm});
            skLineSegment(sketch, "E54.48.7", {"start": v(15.92, 61.1) * mm, "end": v(16.3, 62.78) * mm});
            skArc(sketch, "E54.48.8", {"start": v(15.92, 61.1) * mm, "mid": v(15.26, 60.12) * mm, "end": v(14.53, 59.2) * mm});
            skArc(sketch, "E54.48.9", {"start": v(17.26, 63.37) * mm, "mid": v(16.65, 63.28) * mm, "end": v(16.3, 62.78) * mm});
            skArc(sketch, "E54.49.0", {"start": v(4.27, 64.68) * mm, "mid": v(4.09, 65.27) * mm, "end": v(3.53, 65.54) * mm});
            skLineSegment(sketch, "E54.49.1", {"start": v(4.11, 62.97) * mm, "end": v(4.27, 64.68) * mm});
            skArc(sketch, "E54.49.2", {"start": v(4.11, 62.97) * mm, "mid": v(4.44, 61.83) * mm, "end": v(4.84, 60.73) * mm});
            skArc(sketch, "E54.49.3", {"start": v(4.84, 60.73) * mm, "mid": v(5.1, 60.4) * mm, "end": v(5.47, 60.25) * mm});
            skLineSegment(sketch, "E54.49.4", {"start": v(5.47, 60.25) * mm, "end": v(5.85, 60.2) * mm});
            skLineSegment(sketch, "E54.49.5", {"start": v(6.24, 60.17) * mm, "end": v(5.85, 60.2) * mm});
            skArc(sketch, "E54.49.6", {"start": v(6.24, 60.17) * mm, "mid": v(6.64, 60.26) * mm, "end": v(6.94, 60.53) * mm});
            skLineSegment(sketch, "E54.49.7", {"start": v(8.08, 62.6) * mm, "end": v(8.24, 64.3) * mm});
            skArc(sketch, "E54.49.8", {"start": v(8.08, 62.6) * mm, "mid": v(7.55, 61.54) * mm, "end": v(6.94, 60.53) * mm});
            skArc(sketch, "E54.49.9", {"start": v(9.14, 65.01) * mm, "mid": v(8.54, 64.85) * mm, "end": v(8.24, 64.3) * mm});
            skArc(sketch, "E55.trimOffspring", {"start": v(-12.98, 64.32) * mm, "mid": v(-14.28, 64.04) * mm, "end": v(-15.58, 63.74) * mm});
            skArc(sketch, "E56.trimOffspring", {"start": v(-20.99, 62.16) * mm, "mid": v(-22.25, 61.73) * mm, "end": v(-23.5, 61.26) * mm});
            skArc(sketch, "E57.trimOffspring", {"start": v(-28.66, 59.02) * mm, "mid": v(-29.86, 58.43) * mm, "end": v(-31.04, 57.81) * mm});
            skArc(sketch, "E58.trimOffspring", {"start": v(-35.89, 54.95) * mm, "mid": v(-37, 54.2) * mm, "end": v(-38.1, 53.45) * mm});
            skArc(sketch, "E59.trimOffspring", {"start": v(-42.54, 50) * mm, "mid": v(-43.55, 49.13) * mm, "end": v(-44.54, 48.24) * mm});
            skArc(sketch, "E60.trimOffspring", {"start": v(-48.52, 44.25) * mm, "mid": v(-49.41, 43.26) * mm, "end": v(-50.28, 42.25) * mm});
            skArc(sketch, "E61.trimOffspring", {"start": v(-53.74, 37.8) * mm, "mid": v(-54.5, 36.7) * mm, "end": v(-55.23, 35.6) * mm});
            skArc(sketch, "E62.trimOffspring", {"start": v(-58.1, 30.75) * mm, "mid": v(-58.72, 29.57) * mm, "end": v(-59.31, 28.38) * mm});
            skArc(sketch, "E63.trimOffspring", {"start": v(-61.55, 23.2) * mm, "mid": v(-62.01, 21.96) * mm, "end": v(-62.45, 20.7) * mm});
            skArc(sketch, "E64.trimOffspring", {"start": v(-64.02, 15.3) * mm, "mid": v(-64.33, 14) * mm, "end": v(-64.6, 12.7) * mm});
            skArc(sketch, "E65.trimOffspring", {"start": v(-65.48, 7.13) * mm, "mid": v(-65.62, 5.8) * mm, "end": v(-65.74, 4.48) * mm});
            skArc(sketch, "E66.trimOffspring", {"start": v(-65.91, -1.15) * mm, "mid": v(-65.88, -2.48) * mm, "end": v(-65.83, -3.82) * mm});
            skArc(sketch, "E67.trimOffspring", {"start": v(-65.3, -9.42) * mm, "mid": v(-65.1, -10.74) * mm, "end": v(-64.88, -12.06) * mm});
            skArc(sketch, "E68.trimOffspring", {"start": v(-63.65, -17.55) * mm, "mid": v(-63.3, -18.84) * mm, "end": v(-62.9, -20.11) * mm});
            skArc(sketch, "E69.trimOffspring", {"start": v(-61, -25.4) * mm, "mid": v(-60.48, -26.64) * mm, "end": v(-59.94, -27.86) * mm});
            skArc(sketch, "E70.trimOffspring", {"start": v(-57.39, -32.87) * mm, "mid": v(-56.72, -34.03) * mm, "end": v(-56.03, -35.17) * mm});
            skArc(sketch, "E71.trimOffspring", {"start": v(-52.86, -39.83) * mm, "mid": v(-52.06, -40.89) * mm, "end": v(-51.23, -41.93) * mm});
            skArc(sketch, "E72.trimOffspring", {"start": v(-47.5, -46.16) * mm, "mid": v(-46.57, -47.1) * mm, "end": v(-45.62, -48.04) * mm});
            skArc(sketch, "E73.trimOffspring", {"start": v(-41.4, -51.76) * mm, "mid": v(-40.35, -52.6) * mm, "end": v(-39.3, -53.4) * mm});
            skArc(sketch, "E74.trimOffspring", {"start": v(-34.63, -56.56) * mm, "mid": v(-33.5, -57.25) * mm, "end": v(-32.34, -57.92) * mm});
            skArc(sketch, "E75.trimOffspring", {"start": v(-27.32, -60.48) * mm, "mid": v(-26.1, -61.02) * mm, "end": v(-24.88, -61.54) * mm});
            skArc(sketch, "E76.trimOffspring", {"start": v(-19.58, -63.44) * mm, "mid": v(-18.3, -63.83) * mm, "end": v(-17.02, -64.19) * mm});
            skArc(sketch, "E77.trimOffspring", {"start": v(-11.52, -65.42) * mm, "mid": v(-10.2, -65.64) * mm, "end": v(-8.89, -65.83) * mm});
            skArc(sketch, "E78.trimOffspring", {"start": v(-3.28, -66.36) * mm, "mid": v(-1.95, -66.42) * mm, "end": v(-0.62, -66.45) * mm});
            skArc(sketch, "E79.trimOffspring", {"start": v(5.01, -66.27) * mm, "mid": v(6.34, -66.16) * mm, "end": v(7.66, -66.02) * mm});
            skArc(sketch, "E80.trimOffspring", {"start": v(13.23, -65.14) * mm, "mid": v(14.53, -64.86) * mm, "end": v(15.83, -64.56) * mm});
            skArc(sketch, "E81.trimOffspring", {"start": v(21.24, -62.99) * mm, "mid": v(22.5, -62.55) * mm, "end": v(23.74, -62.08) * mm});
            skArc(sketch, "E82.trimOffspring", {"start": v(28.91, -59.85) * mm, "mid": v(30.1, -59.25) * mm, "end": v(31.29, -58.64) * mm});
            skArc(sketch, "E83.trimOffspring", {"start": v(36.13, -55.77) * mm, "mid": v(37.24, -55.03) * mm, "end": v(38.34, -54.27) * mm});
            skArc(sketch, "E84.trimOffspring", {"start": v(42.79, -50.82) * mm, "mid": v(43.8, -49.95) * mm, "end": v(44.79, -49.06) * mm});
            skArc(sketch, "E85.trimOffspring", {"start": v(48.77, -45.07) * mm, "mid": v(49.66, -44.08) * mm, "end": v(50.53, -43.07) * mm});
            skArc(sketch, "E86.trimOffspring", {"start": v(53.98, -38.63) * mm, "mid": v(54.74, -37.53) * mm, "end": v(55.48, -36.42) * mm});
            skArc(sketch, "E87.trimOffspring", {"start": v(58.35, -31.57) * mm, "mid": v(58.97, -30.4) * mm, "end": v(59.56, -29.2) * mm});
            skArc(sketch, "E88.trimOffspring", {"start": v(61.8, -24.03) * mm, "mid": v(62.26, -22.78) * mm, "end": v(62.7, -21.52) * mm});
            skArc(sketch, "E89.trimOffspring", {"start": v(64.27, -16.11) * mm, "mid": v(64.57, -14.82) * mm, "end": v(64.85, -13.51) * mm});
            skArc(sketch, "E90.trimOffspring", {"start": v(65.73, -7.95) * mm, "mid": v(65.87, -6.63) * mm, "end": v(65.98, -5.3) * mm});
            skArc(sketch, "E91.trimOffspring", {"start": v(66.16, 0.33) * mm, "mid": v(66.13, 1.66) * mm, "end": v(66.08, 3) * mm});
            skArc(sketch, "E92.trimOffspring", {"start": v(65.55, 8.6) * mm, "mid": v(65.35, 9.92) * mm, "end": v(65.13, 11.23) * mm});
            skArc(sketch, "E93.trimOffspring", {"start": v(63.9, 16.73) * mm, "mid": v(63.54, 18.01) * mm, "end": v(63.16, 19.3) * mm});
            skArc(sketch, "E94.trimOffspring", {"start": v(57.63, 32.05) * mm, "mid": v(56.97, 33.2) * mm, "end": v(56.28, 34.35) * mm});
            skArc(sketch, "E95.trimOffspring", {"start": v(53.11, 39) * mm, "mid": v(52.3, 40.07) * mm, "end": v(51.48, 41.11) * mm});
            skArc(sketch, "E96.trimOffspring", {"start": v(47.75, 45.33) * mm, "mid": v(46.82, 46.29) * mm, "end": v(45.87, 47.22) * mm});
            skArc(sketch, "E97.trimOffspring", {"start": v(41.65, 50.94) * mm, "mid": v(40.6, 51.77) * mm, "end": v(39.54, 52.58) * mm});
            skArc(sketch, "E98.trimOffspring", {"start": v(34.88, 55.74) * mm, "mid": v(33.74, 56.43) * mm, "end": v(32.59, 57.1) * mm});
            skArc(sketch, "E99.trimOffspring", {"start": v(27.57, 59.66) * mm, "mid": v(26.35, 60.2) * mm, "end": v(25.12, 60.71) * mm});
            skArc(sketch, "E100.trimOffspring", {"start": v(19.82, 62.62) * mm, "mid": v(18.55, 63) * mm, "end": v(17.26, 63.37) * mm});
            skArc(sketch, "E101.trimOffspring", {"start": v(11.77, 64.6) * mm, "mid": v(10.45, 64.82) * mm, "end": v(9.14, 65.01) * mm});
            skArc(sketch, "E102.trimOffspring", {"start": v(3.53, 65.54) * mm, "mid": v(2.2, 65.6) * mm, "end": v(0.87, 65.63) * mm});
            skLineSegment(sketch, "E103", {"start": v(60.2, 27.03) * mm, "end": v(61.25, 24.59) * mm});
            skSolve(sketch);
        }
        {
            var Q0;
            Q0=makeQuery(id+"F0.imprint","IMPRINT",FACE,{"disambiguationData":[TD([[makeQuery(id+"F0.imprint","IMPRINT",EDGE,{"derivedFrom":sQuery(id+"F0.wireOp",EDGE,"E0")}),1.0]])]});
            extrude(context, id + "F1", {"entities" : qUnion([Q0]), "depth" : 127 * mm});
        }
    });
